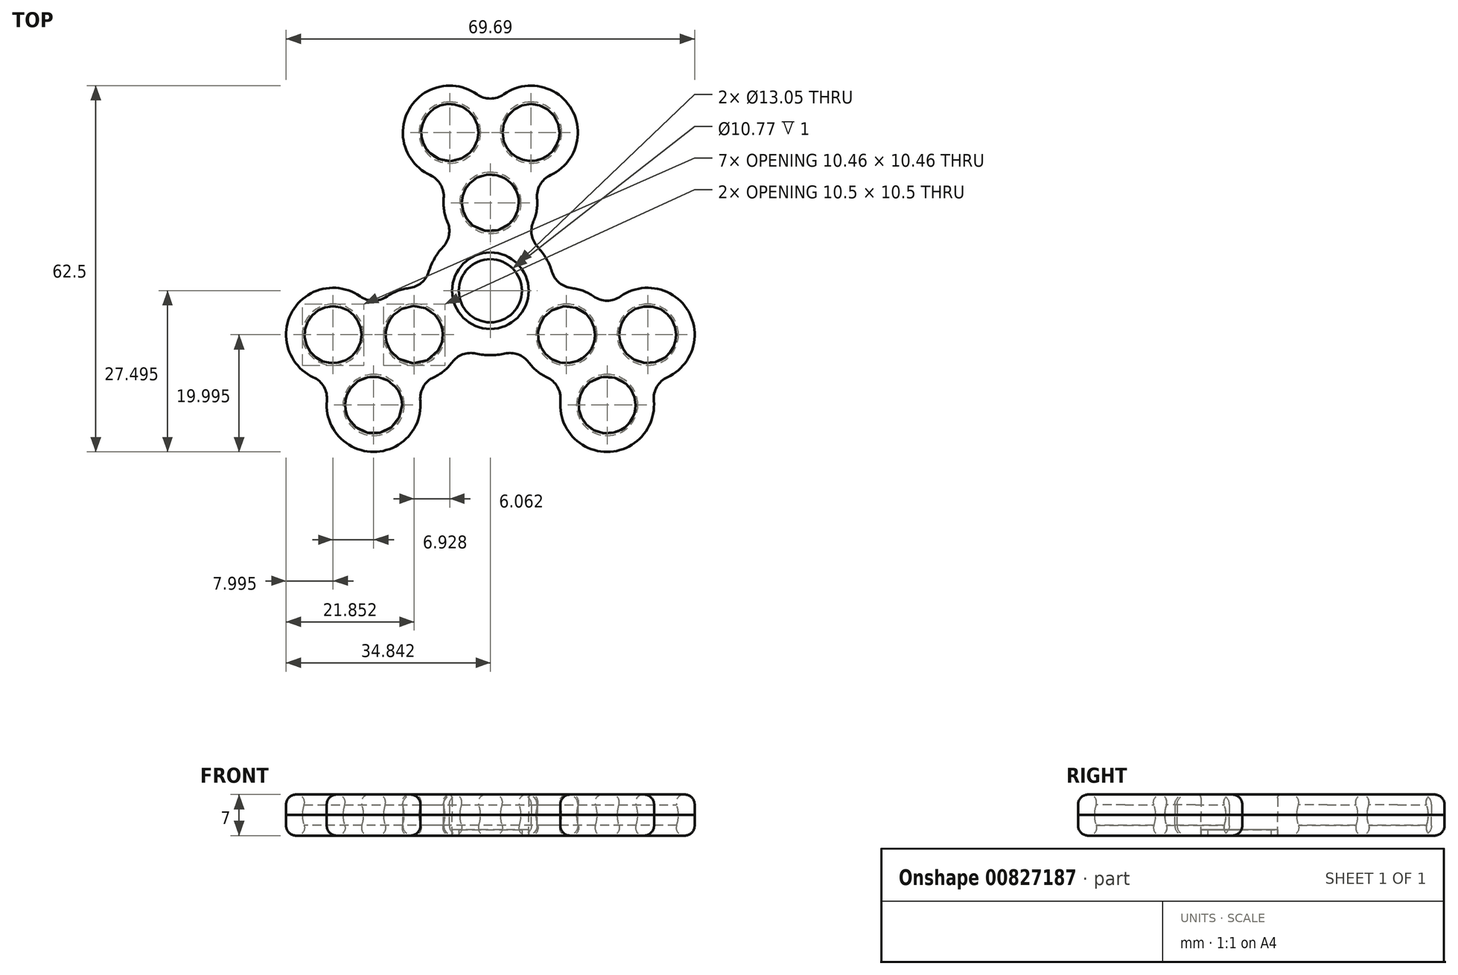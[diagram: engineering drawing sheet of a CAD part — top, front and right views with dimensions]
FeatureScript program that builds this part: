
annotation { "Feature Type Name" : "Feature", "Feature Type Description" : "" }
export const myFeature = defineFeature(function(context is Context, id is Id, definition is map)
    precondition{}
    {
        {
            var Q0;
            Q0=qCreatedBy(makeId("Top.planeOp"),FACE);
            var sketch = newSketch(context, id + "F0", { "sketchPlane" : qUnion([Q0])});
            skCircle(sketch, "E0", {"center": v(73.24, 0.6) * mm, "radius": 6.53 * mm});
            skCircle(sketch, "E1", {"center": v(73.24, 15.6) * mm, "radius": 2.5 * mm});
            skCircle(sketch, "E2", {"center": v(60.25, -6.9) * mm, "radius": 2.5 * mm});
            skCircle(sketch, "E3", {"center": v(86.23, -6.9) * mm, "radius": 2.5 * mm});
            skCircle(sketch, "E4", {"center": v(80.17, 27.6) * mm, "radius": 2.5 * mm});
            skCircle(sketch, "E5", {"center": v(66.31, 27.6) * mm, "radius": 2.5 * mm});
            skCircle(sketch, "E6", {"center": v(46.4, -6.9) * mm, "radius": 2.5 * mm});
            skCircle(sketch, "E7", {"center": v(53.32, -18.9) * mm, "radius": 2.5 * mm});
            skCircle(sketch, "E8", {"center": v(93.16, -18.9) * mm, "radius": 2.5 * mm});
            skCircle(sketch, "E9", {"center": v(100.09, -6.9) * mm, "radius": 2.5 * mm});
            skPoint(sketch, "E10.visualSharp", {"position": v(73.24, 28.6) * mm});
            skPoint(sketch, "E11.visualSharp", {"position": v(68.91, 21.1) * mm});
            skPoint(sketch, "E12.visualSharp", {"position": v(77.57, 21.1) * mm});
            skPoint(sketch, "E13.visualSharp", {"position": v(63.31, -0.6) * mm});
            skPoint(sketch, "E14.visualSharp", {"position": v(67.23, -7.39) * mm});
            skPoint(sketch, "E15.visualSharp", {"position": v(79.25, -7.39) * mm});
            skPoint(sketch, "E16.visualSharp", {"position": v(83.17, -0.6) * mm});
            skPoint(sketch, "E17.visualSharp", {"position": v(77.16, 9.8) * mm});
            skPoint(sketch, "E18.visualSharp", {"position": v(69.32, 9.8) * mm});
            skArc(sketch, "E19.0", {"start": v(59.36, 1.05) * mm, "mid": v(57.4, 0.58) * mm, "end": v(55.63, -0.36) * mm});
            skArc(sketch, "E19.1", {"start": v(65.18, 8.09) * mm, "mid": v(63.72, 6.1) * mm, "end": v(62.73, 3.85) * mm});
            skArc(sketch, "E19.2", {"start": v(65.28, 16.34) * mm, "mid": v(65.34, 14.33) * mm, "end": v(65.9, 12.4) * mm});
            skArc(sketch, "E19.3", {"start": v(70.93, 34.14) * mm, "mid": v(59.39, 31.6) * mm, "end": v(62.97, 20.34) * mm});
            skArc(sketch, "E19.4", {"start": v(79.8, -11.64) * mm, "mid": v(81.18, -13.1) * mm, "end": v(82.88, -14.16) * mm});
            skArc(sketch, "E19.5", {"start": v(70.8, -10.12) * mm, "mid": v(73.24, -10.4) * mm, "end": v(75.69, -10.12) * mm});
            skArc(sketch, "E19.6", {"start": v(63.6, -14.16) * mm, "mid": v(65.3, -13.1) * mm, "end": v(66.69, -11.64) * mm});
            skArc(sketch, "E19.7", {"start": v(45.36, -18.16) * mm, "mid": v(53.32, -26.9) * mm, "end": v(61.29, -18.16) * mm});
            skArc(sketch, "E19.8", {"start": v(85.2, -18.16) * mm, "mid": v(93.16, -26.9) * mm, "end": v(101.13, -18.16) * mm});
            skArc(sketch, "E19.9", {"start": v(103.44, -14.16) * mm, "mid": v(107.02, -2.9) * mm, "end": v(95.47, -0.36) * mm});
            skArc(sketch, "E19.10", {"start": v(90.85, -0.36) * mm, "mid": v(89.08, 0.58) * mm, "end": v(87.13, 1.05) * mm});
            skArc(sketch, "E19.11", {"start": v(83.75, 3.85) * mm, "mid": v(82.77, 6.1) * mm, "end": v(81.3, 8.09) * mm});
            skArc(sketch, "E19.12", {"start": v(51.01, -0.36) * mm, "mid": v(39.47, -2.9) * mm, "end": v(43.05, -14.16) * mm});
            skArc(sketch, "E19.13", {"start": v(80.57, 12.4) * mm, "mid": v(81.14, 14.33) * mm, "end": v(81.2, 16.34) * mm});
            skArc(sketch, "E19.14", {"start": v(83.52, 20.34) * mm, "mid": v(87.1, 31.6) * mm, "end": v(75.55, 34.14) * mm});
            skArc(sketch, "E20.0", {"start": v(45.36, -18.16) * mm, "mid": v(44.84, -15.8) * mm, "end": v(43.05, -14.16) * mm});
            skArc(sketch, "E21.0", {"start": v(63.6, -14.16) * mm, "mid": v(61.8, -15.8) * mm, "end": v(61.29, -18.16) * mm});
            skArc(sketch, "E22.0", {"start": v(70.8, -10.12) * mm, "mid": v(68.52, -10.27) * mm, "end": v(66.69, -11.64) * mm});
            skArc(sketch, "E23.0", {"start": v(79.8, -11.64) * mm, "mid": v(77.97, -10.27) * mm, "end": v(75.69, -10.12) * mm});
            skArc(sketch, "E24.0", {"start": v(85.2, -18.16) * mm, "mid": v(84.68, -15.8) * mm, "end": v(82.88, -14.16) * mm});
            skArc(sketch, "E25.0", {"start": v(103.44, -14.16) * mm, "mid": v(101.65, -15.8) * mm, "end": v(101.13, -18.16) * mm});
            skArc(sketch, "E26.0", {"start": v(90.85, -0.36) * mm, "mid": v(93.16, -1.1) * mm, "end": v(95.47, -0.36) * mm});
            skArc(sketch, "E27.0", {"start": v(83.75, 3.85) * mm, "mid": v(85.02, 1.95) * mm, "end": v(87.13, 1.05) * mm});
            skArc(sketch, "E28.0", {"start": v(80.57, 12.4) * mm, "mid": v(80.3, 10.14) * mm, "end": v(81.3, 8.09) * mm});
            skArc(sketch, "E29.0", {"start": v(83.52, 20.34) * mm, "mid": v(81.73, 18.7) * mm, "end": v(81.2, 16.34) * mm});
            skArc(sketch, "E30.0", {"start": v(65.28, 16.34) * mm, "mid": v(64.76, 18.7) * mm, "end": v(62.97, 20.34) * mm});
            skArc(sketch, "E31.0", {"start": v(65.18, 8.09) * mm, "mid": v(66.19, 10.14) * mm, "end": v(65.9, 12.4) * mm});
            skArc(sketch, "E32.0", {"start": v(59.36, 1.05) * mm, "mid": v(61.46, 1.95) * mm, "end": v(62.73, 3.85) * mm});
            skArc(sketch, "E33.0", {"start": v(51.01, -0.36) * mm, "mid": v(53.32, -1.1) * mm, "end": v(55.63, -0.36) * mm});
            skArc(sketch, "E34.0", {"start": v(70.93, 34.14) * mm, "mid": v(73.24, 33.4) * mm, "end": v(75.55, 34.14) * mm});
            skSolve(sketch);
        }
        {
            var Q0;
            Q0=qSketchRegion(id+"F0",true);
            extrude(context, id + "F1", {"entities" : qUnion([Q0]), "depth" : 3.5 * mm, "offsetDistance" : 25 * mm});
        }
        {
            var Q0;
            Q0=makeQuery(id+"F0.imprint","IMPRINT",FACE,{"disambiguationData":[TD([[makeQuery(id+"F0.imprint","IMPRINT",EDGE,{"derivedFrom":sQuery(id+"F0.wireOp",EDGE,"E0")}),-1.0]])]});
            extrude(context, id + "F2", {"entities" : qUnion([Q0]), "oppositeDirection" : true, "depth" : 3.5 * mm, "offsetDistance" : 25 * mm});
        }
        {
            var Q0;
            Q0=makeQuery(id+"F2.opExtrude","CAP_FACE",FACE,{"disambiguationData":[OSD([sQuery(id+"F0.wireOp",EDGE,"E0"),sQuery(id+"F0.wireOp",EDGE,"tXCEuyxa-6lNA-QPCA-4HXf-ApKYShcEb0Yf"),sQuery(id+"F0.wireOp",EDGE,"E1"),sQuery(id+"F0.wireOp",EDGE,"E2"),sQuery(id+"F0.wireOp",EDGE,"E3"),sQuery(id+"F0.wireOp",EDGE,"E4"),sQuery(id+"F0.wireOp",EDGE,"E5"),sQuery(id+"F0.wireOp",EDGE,"E6"),sQuery(id+"F0.wireOp",EDGE,"E7"),sQuery(id+"F0.wireOp",EDGE,"E8"),sQuery(id+"F0.wireOp",EDGE,"E9"),sQuery(id+"F0.wireOp",EDGE,"0kcF6Lq4-WqBE-dODE-wINV-nyZN5JArXVcS"),sQuery(id+"F0.wireOp",EDGE,"VSrMeVpB-pvXp-ETii-wjF9-Px2PqwZYQnOt"),sQuery(id+"F0.wireOp",EDGE,"OGzEMItw-FQCu-QhKJ-kTiP-AlfaDmg1CYfA"),sQuery(id+"F0.wireOp",EDGE,"E10.filletArc"),sQuery(id+"F0.wireOp",EDGE,"E11.filletArc"),sQuery(id+"F0.wireOp",EDGE,"E12.filletArc"),sQuery(id+"F0.wireOp",EDGE,"61869019-6ff7-477d-8c79-2028de4a396b.trimOffspring"),sQuery(id+"F0.wireOp",EDGE,"b39f1e7b-d492-47c6-a918-6e9c5b166b17"),sQuery(id+"F0.wireOp",EDGE,"9a7d06a7-665d-4e92-ad9d-959fca317462"),sQuery(id+"F0.wireOp",EDGE,"db31c51f-78d2-4091-9bd3-34a254103f45"),sQuery(id+"F0.wireOp",EDGE,"aaf24792-0303-4d5f-86de-c3b2a19fc74e.filletArc"),sQuery(id+"F0.wireOp",EDGE,"5ffe84d5-8cdf-4c2e-9e98-3655a6b86056.filletArc"),sQuery(id+"F0.wireOp",EDGE,"e8945d06-678d-4789-81f5-b1335d2624b7.filletArc"),sQuery(id+"F0.wireOp",EDGE,"a0b45458-2819-4e46-80a9-56e3c7e3f3b4.trimOffspring"),sQuery(id+"F0.wireOp",EDGE,"bf295548-413a-4249-b2ed-de7f7c0a0b82"),sQuery(id+"F0.wireOp",EDGE,"b03dbe81-5cdf-4ba7-a8f7-bb7ec46ab3a8"),sQuery(id+"F0.wireOp",EDGE,"b0d05724-446d-4885-847a-915c569f1139"),sQuery(id+"F0.wireOp",EDGE,"608d76ae-a745-4fd0-ae95-f5732494cd55.filletArc"),sQuery(id+"F0.wireOp",EDGE,"a41367dd-7dbd-4f08-888b-74168a8e5936.filletArc"),sQuery(id+"F0.wireOp",EDGE,"84e31002-7089-4eef-81a0-79c8965d61ed.filletArc"),sQuery(id+"F0.wireOp",EDGE,"1335fa2d-2410-4889-a90b-ae026db059b2.trimOffspring"),sQuery(id+"F0.wireOp",EDGE,"81157b49-ae94-446f-8b4e-5ce1e116e724.trimOffspring"),sQuery(id+"F0.wireOp",EDGE,"4f1c551e-3bfd-48a9-873a-6291d27f8455.trimOffspring"),sQuery(id+"F0.wireOp",EDGE,"E13.filletArc"),sQuery(id+"F0.wireOp",EDGE,"E14.filletArc"),sQuery(id+"F0.wireOp",EDGE,"E15.filletArc"),sQuery(id+"F0.wireOp",EDGE,"E16.filletArc"),sQuery(id+"F0.wireOp",EDGE,"E17.filletArc"),sQuery(id+"F0.wireOp",EDGE,"E18.filletArc")])],"isStart":true});
            var sketch = newSketch(context, id + "F3", { "sketchPlane" : qUnion([Q0])});
            skLineSegment(sketch, "E35", {"start": v(53.32, -18.9) * mm, "end": v(53.32, -24.12) * mm});
            skLineSegment(sketch, "E36", {"start": v(53.32, -18.9) * mm, "end": v(53.32, -13.66) * mm});
            skArc(sketch, "E37", {"start": v(53.32, -13.66) * mm, "mid": v(48.1, -18.9) * mm, "end": v(53.32, -24.12) * mm});
            skSolve(sketch);
        }
        {
            var Q0;
            Q0 = qSketchRegion(id + "F3", true);
            var Q1;
            Q1=sQuery(id+"F3.wireOp",EDGE,"E36");
            revolve(context, id + "F4", {"surfaceOperationType" : NewSurfaceOperationType.NEW, "entities" : qUnion([Q0]), "axis" : qUnion([Q1]), "revolveType" : RevolveType.FULL});
        }
        {
            var Q0;
            Q0=makeQuery(id+"F2.opExtrude","CAP_FACE",FACE,{"disambiguationData":[OSD([sQuery(id+"F0.wireOp",EDGE,"E0"),sQuery(id+"F0.wireOp",EDGE,"tXCEuyxa-6lNA-QPCA-4HXf-ApKYShcEb0Yf"),sQuery(id+"F0.wireOp",EDGE,"E1"),sQuery(id+"F0.wireOp",EDGE,"E2"),sQuery(id+"F0.wireOp",EDGE,"E3"),sQuery(id+"F0.wireOp",EDGE,"E4"),sQuery(id+"F0.wireOp",EDGE,"E5"),sQuery(id+"F0.wireOp",EDGE,"E6"),sQuery(id+"F0.wireOp",EDGE,"E7"),sQuery(id+"F0.wireOp",EDGE,"E8"),sQuery(id+"F0.wireOp",EDGE,"E9"),sQuery(id+"F0.wireOp",EDGE,"0kcF6Lq4-WqBE-dODE-wINV-nyZN5JArXVcS"),sQuery(id+"F0.wireOp",EDGE,"VSrMeVpB-pvXp-ETii-wjF9-Px2PqwZYQnOt"),sQuery(id+"F0.wireOp",EDGE,"OGzEMItw-FQCu-QhKJ-kTiP-AlfaDmg1CYfA"),sQuery(id+"F0.wireOp",EDGE,"E10.filletArc"),sQuery(id+"F0.wireOp",EDGE,"E11.filletArc"),sQuery(id+"F0.wireOp",EDGE,"E12.filletArc"),sQuery(id+"F0.wireOp",EDGE,"61869019-6ff7-477d-8c79-2028de4a396b.trimOffspring"),sQuery(id+"F0.wireOp",EDGE,"b39f1e7b-d492-47c6-a918-6e9c5b166b17"),sQuery(id+"F0.wireOp",EDGE,"9a7d06a7-665d-4e92-ad9d-959fca317462"),sQuery(id+"F0.wireOp",EDGE,"db31c51f-78d2-4091-9bd3-34a254103f45"),sQuery(id+"F0.wireOp",EDGE,"aaf24792-0303-4d5f-86de-c3b2a19fc74e.filletArc"),sQuery(id+"F0.wireOp",EDGE,"5ffe84d5-8cdf-4c2e-9e98-3655a6b86056.filletArc"),sQuery(id+"F0.wireOp",EDGE,"e8945d06-678d-4789-81f5-b1335d2624b7.filletArc"),sQuery(id+"F0.wireOp",EDGE,"a0b45458-2819-4e46-80a9-56e3c7e3f3b4.trimOffspring"),sQuery(id+"F0.wireOp",EDGE,"bf295548-413a-4249-b2ed-de7f7c0a0b82"),sQuery(id+"F0.wireOp",EDGE,"b03dbe81-5cdf-4ba7-a8f7-bb7ec46ab3a8"),sQuery(id+"F0.wireOp",EDGE,"b0d05724-446d-4885-847a-915c569f1139"),sQuery(id+"F0.wireOp",EDGE,"608d76ae-a745-4fd0-ae95-f5732494cd55.filletArc"),sQuery(id+"F0.wireOp",EDGE,"a41367dd-7dbd-4f08-888b-74168a8e5936.filletArc"),sQuery(id+"F0.wireOp",EDGE,"84e31002-7089-4eef-81a0-79c8965d61ed.filletArc"),sQuery(id+"F0.wireOp",EDGE,"1335fa2d-2410-4889-a90b-ae026db059b2.trimOffspring"),sQuery(id+"F0.wireOp",EDGE,"81157b49-ae94-446f-8b4e-5ce1e116e724.trimOffspring"),sQuery(id+"F0.wireOp",EDGE,"4f1c551e-3bfd-48a9-873a-6291d27f8455.trimOffspring"),sQuery(id+"F0.wireOp",EDGE,"E13.filletArc"),sQuery(id+"F0.wireOp",EDGE,"E14.filletArc"),sQuery(id+"F0.wireOp",EDGE,"E15.filletArc"),sQuery(id+"F0.wireOp",EDGE,"E16.filletArc"),sQuery(id+"F0.wireOp",EDGE,"E17.filletArc"),sQuery(id+"F0.wireOp",EDGE,"E18.filletArc")])],"isStart":true});
            var sketch = newSketch(context, id + "F5", { "sketchPlane" : qUnion([Q0])});
            skLineSegment(sketch, "E38", {"start": v(60.25, -6.9) * mm, "end": v(60.25, -12.14) * mm});
            skLineSegment(sketch, "E39", {"start": v(60.25, -6.9) * mm, "end": v(60.25, -1.64) * mm});
            skArc(sketch, "E40", {"start": v(60.25, -1.64) * mm, "mid": v(55, -6.9) * mm, "end": v(60.25, -12.14) * mm});
            skSolve(sketch);
        }
        {
            var Q0;
            Q0=makeQuery(id+"F2.opExtrude","CAP_FACE",FACE,{"disambiguationData":[OSD([sQuery(id+"F0.wireOp",EDGE,"E0"),sQuery(id+"F0.wireOp",EDGE,"tXCEuyxa-6lNA-QPCA-4HXf-ApKYShcEb0Yf"),sQuery(id+"F0.wireOp",EDGE,"E1"),sQuery(id+"F0.wireOp",EDGE,"E2"),sQuery(id+"F0.wireOp",EDGE,"E3"),sQuery(id+"F0.wireOp",EDGE,"E4"),sQuery(id+"F0.wireOp",EDGE,"E5"),sQuery(id+"F0.wireOp",EDGE,"E6"),sQuery(id+"F0.wireOp",EDGE,"E7"),sQuery(id+"F0.wireOp",EDGE,"E8"),sQuery(id+"F0.wireOp",EDGE,"E9"),sQuery(id+"F0.wireOp",EDGE,"0kcF6Lq4-WqBE-dODE-wINV-nyZN5JArXVcS"),sQuery(id+"F0.wireOp",EDGE,"VSrMeVpB-pvXp-ETii-wjF9-Px2PqwZYQnOt"),sQuery(id+"F0.wireOp",EDGE,"OGzEMItw-FQCu-QhKJ-kTiP-AlfaDmg1CYfA"),sQuery(id+"F0.wireOp",EDGE,"E10.filletArc"),sQuery(id+"F0.wireOp",EDGE,"E11.filletArc"),sQuery(id+"F0.wireOp",EDGE,"E12.filletArc"),sQuery(id+"F0.wireOp",EDGE,"61869019-6ff7-477d-8c79-2028de4a396b.trimOffspring"),sQuery(id+"F0.wireOp",EDGE,"b39f1e7b-d492-47c6-a918-6e9c5b166b17"),sQuery(id+"F0.wireOp",EDGE,"9a7d06a7-665d-4e92-ad9d-959fca317462"),sQuery(id+"F0.wireOp",EDGE,"db31c51f-78d2-4091-9bd3-34a254103f45"),sQuery(id+"F0.wireOp",EDGE,"aaf24792-0303-4d5f-86de-c3b2a19fc74e.filletArc"),sQuery(id+"F0.wireOp",EDGE,"5ffe84d5-8cdf-4c2e-9e98-3655a6b86056.filletArc"),sQuery(id+"F0.wireOp",EDGE,"e8945d06-678d-4789-81f5-b1335d2624b7.filletArc"),sQuery(id+"F0.wireOp",EDGE,"a0b45458-2819-4e46-80a9-56e3c7e3f3b4.trimOffspring"),sQuery(id+"F0.wireOp",EDGE,"bf295548-413a-4249-b2ed-de7f7c0a0b82"),sQuery(id+"F0.wireOp",EDGE,"b03dbe81-5cdf-4ba7-a8f7-bb7ec46ab3a8"),sQuery(id+"F0.wireOp",EDGE,"b0d05724-446d-4885-847a-915c569f1139"),sQuery(id+"F0.wireOp",EDGE,"608d76ae-a745-4fd0-ae95-f5732494cd55.filletArc"),sQuery(id+"F0.wireOp",EDGE,"a41367dd-7dbd-4f08-888b-74168a8e5936.filletArc"),sQuery(id+"F0.wireOp",EDGE,"84e31002-7089-4eef-81a0-79c8965d61ed.filletArc"),sQuery(id+"F0.wireOp",EDGE,"1335fa2d-2410-4889-a90b-ae026db059b2.trimOffspring"),sQuery(id+"F0.wireOp",EDGE,"81157b49-ae94-446f-8b4e-5ce1e116e724.trimOffspring"),sQuery(id+"F0.wireOp",EDGE,"4f1c551e-3bfd-48a9-873a-6291d27f8455.trimOffspring"),sQuery(id+"F0.wireOp",EDGE,"E13.filletArc"),sQuery(id+"F0.wireOp",EDGE,"E14.filletArc"),sQuery(id+"F0.wireOp",EDGE,"E15.filletArc"),sQuery(id+"F0.wireOp",EDGE,"E16.filletArc"),sQuery(id+"F0.wireOp",EDGE,"E17.filletArc"),sQuery(id+"F0.wireOp",EDGE,"E18.filletArc")])],"isStart":true});
            var sketch = newSketch(context, id + "F6", { "sketchPlane" : qUnion([Q0])});
            skLineSegment(sketch, "E41", {"start": v(93.16, -18.9) * mm, "end": v(93.16, -24.12) * mm});
            skArc(sketch, "E42", {"start": v(93.16, -13.66) * mm, "mid": v(87.93, -18.9) * mm, "end": v(93.16, -24.12) * mm});
            skLineSegment(sketch, "E43", {"start": v(93.16, -18.9) * mm, "end": v(93.16, -13.66) * mm});
            skSolve(sketch);
        }
        {
            var Q0;
            Q0 = qSketchRegion(id + "F6", true);
            var Q1;
            Q1=sQuery(id+"F6.wireOp",EDGE,"E43");
            revolve(context, id + "F7", {"surfaceOperationType" : NewSurfaceOperationType.NEW, "entities" : qUnion([Q0]), "axis" : qUnion([Q1]), "revolveType" : RevolveType.FULL});
        }
        {
            var Q0;
            Q0=makeQuery(id+"F2.opExtrude","CAP_FACE",FACE,{"disambiguationData":[OSD([sQuery(id+"F0.wireOp",EDGE,"E0"),sQuery(id+"F0.wireOp",EDGE,"tXCEuyxa-6lNA-QPCA-4HXf-ApKYShcEb0Yf"),sQuery(id+"F0.wireOp",EDGE,"E1"),sQuery(id+"F0.wireOp",EDGE,"E2"),sQuery(id+"F0.wireOp",EDGE,"E3"),sQuery(id+"F0.wireOp",EDGE,"E4"),sQuery(id+"F0.wireOp",EDGE,"E5"),sQuery(id+"F0.wireOp",EDGE,"E6"),sQuery(id+"F0.wireOp",EDGE,"E7"),sQuery(id+"F0.wireOp",EDGE,"E8"),sQuery(id+"F0.wireOp",EDGE,"E9"),sQuery(id+"F0.wireOp",EDGE,"0kcF6Lq4-WqBE-dODE-wINV-nyZN5JArXVcS"),sQuery(id+"F0.wireOp",EDGE,"VSrMeVpB-pvXp-ETii-wjF9-Px2PqwZYQnOt"),sQuery(id+"F0.wireOp",EDGE,"OGzEMItw-FQCu-QhKJ-kTiP-AlfaDmg1CYfA"),sQuery(id+"F0.wireOp",EDGE,"E10.filletArc"),sQuery(id+"F0.wireOp",EDGE,"E11.filletArc"),sQuery(id+"F0.wireOp",EDGE,"E12.filletArc"),sQuery(id+"F0.wireOp",EDGE,"61869019-6ff7-477d-8c79-2028de4a396b.trimOffspring"),sQuery(id+"F0.wireOp",EDGE,"b39f1e7b-d492-47c6-a918-6e9c5b166b17"),sQuery(id+"F0.wireOp",EDGE,"9a7d06a7-665d-4e92-ad9d-959fca317462"),sQuery(id+"F0.wireOp",EDGE,"db31c51f-78d2-4091-9bd3-34a254103f45"),sQuery(id+"F0.wireOp",EDGE,"aaf24792-0303-4d5f-86de-c3b2a19fc74e.filletArc"),sQuery(id+"F0.wireOp",EDGE,"5ffe84d5-8cdf-4c2e-9e98-3655a6b86056.filletArc"),sQuery(id+"F0.wireOp",EDGE,"e8945d06-678d-4789-81f5-b1335d2624b7.filletArc"),sQuery(id+"F0.wireOp",EDGE,"a0b45458-2819-4e46-80a9-56e3c7e3f3b4.trimOffspring"),sQuery(id+"F0.wireOp",EDGE,"bf295548-413a-4249-b2ed-de7f7c0a0b82"),sQuery(id+"F0.wireOp",EDGE,"b03dbe81-5cdf-4ba7-a8f7-bb7ec46ab3a8"),sQuery(id+"F0.wireOp",EDGE,"b0d05724-446d-4885-847a-915c569f1139"),sQuery(id+"F0.wireOp",EDGE,"608d76ae-a745-4fd0-ae95-f5732494cd55.filletArc"),sQuery(id+"F0.wireOp",EDGE,"a41367dd-7dbd-4f08-888b-74168a8e5936.filletArc"),sQuery(id+"F0.wireOp",EDGE,"84e31002-7089-4eef-81a0-79c8965d61ed.filletArc"),sQuery(id+"F0.wireOp",EDGE,"1335fa2d-2410-4889-a90b-ae026db059b2.trimOffspring"),sQuery(id+"F0.wireOp",EDGE,"81157b49-ae94-446f-8b4e-5ce1e116e724.trimOffspring"),sQuery(id+"F0.wireOp",EDGE,"4f1c551e-3bfd-48a9-873a-6291d27f8455.trimOffspring"),sQuery(id+"F0.wireOp",EDGE,"E13.filletArc"),sQuery(id+"F0.wireOp",EDGE,"E14.filletArc"),sQuery(id+"F0.wireOp",EDGE,"E15.filletArc"),sQuery(id+"F0.wireOp",EDGE,"E16.filletArc"),sQuery(id+"F0.wireOp",EDGE,"E17.filletArc"),sQuery(id+"F0.wireOp",EDGE,"E18.filletArc")])],"isStart":true});
            var sketch = newSketch(context, id + "F8", { "sketchPlane" : qUnion([Q0])});
            skLineSegment(sketch, "E44", {"start": v(86.23, -6.9) * mm, "end": v(86.23, -12.12) * mm});
            skArc(sketch, "E45", {"start": v(86.23, -1.66) * mm, "mid": v(81, -6.9) * mm, "end": v(86.23, -12.12) * mm});
            skLineSegment(sketch, "E46", {"start": v(86.23, -6.9) * mm, "end": v(86.23, -1.66) * mm});
            skSolve(sketch);
        }
        {
            var Q0;
            Q0 = qSketchRegion(id + "F8", true);
            var Q1;
            Q1=sQuery(id+"F8.wireOp",EDGE,"E46");
            revolve(context, id + "F9", {"surfaceOperationType" : NewSurfaceOperationType.NEW, "entities" : qUnion([Q0]), "axis" : qUnion([Q1]), "revolveType" : RevolveType.FULL});
        }
        {
            var Q0;
            Q0=makeQuery(id+"F2.opExtrude","CAP_FACE",FACE,{"disambiguationData":[OSD([sQuery(id+"F0.wireOp",EDGE,"E0"),sQuery(id+"F0.wireOp",EDGE,"tXCEuyxa-6lNA-QPCA-4HXf-ApKYShcEb0Yf"),sQuery(id+"F0.wireOp",EDGE,"E1"),sQuery(id+"F0.wireOp",EDGE,"E2"),sQuery(id+"F0.wireOp",EDGE,"E3"),sQuery(id+"F0.wireOp",EDGE,"E4"),sQuery(id+"F0.wireOp",EDGE,"E5"),sQuery(id+"F0.wireOp",EDGE,"E6"),sQuery(id+"F0.wireOp",EDGE,"E7"),sQuery(id+"F0.wireOp",EDGE,"E8"),sQuery(id+"F0.wireOp",EDGE,"E9"),sQuery(id+"F0.wireOp",EDGE,"0kcF6Lq4-WqBE-dODE-wINV-nyZN5JArXVcS"),sQuery(id+"F0.wireOp",EDGE,"VSrMeVpB-pvXp-ETii-wjF9-Px2PqwZYQnOt"),sQuery(id+"F0.wireOp",EDGE,"OGzEMItw-FQCu-QhKJ-kTiP-AlfaDmg1CYfA"),sQuery(id+"F0.wireOp",EDGE,"E10.filletArc"),sQuery(id+"F0.wireOp",EDGE,"E11.filletArc"),sQuery(id+"F0.wireOp",EDGE,"E12.filletArc"),sQuery(id+"F0.wireOp",EDGE,"61869019-6ff7-477d-8c79-2028de4a396b.trimOffspring"),sQuery(id+"F0.wireOp",EDGE,"b39f1e7b-d492-47c6-a918-6e9c5b166b17"),sQuery(id+"F0.wireOp",EDGE,"9a7d06a7-665d-4e92-ad9d-959fca317462"),sQuery(id+"F0.wireOp",EDGE,"db31c51f-78d2-4091-9bd3-34a254103f45"),sQuery(id+"F0.wireOp",EDGE,"aaf24792-0303-4d5f-86de-c3b2a19fc74e.filletArc"),sQuery(id+"F0.wireOp",EDGE,"5ffe84d5-8cdf-4c2e-9e98-3655a6b86056.filletArc"),sQuery(id+"F0.wireOp",EDGE,"e8945d06-678d-4789-81f5-b1335d2624b7.filletArc"),sQuery(id+"F0.wireOp",EDGE,"a0b45458-2819-4e46-80a9-56e3c7e3f3b4.trimOffspring"),sQuery(id+"F0.wireOp",EDGE,"bf295548-413a-4249-b2ed-de7f7c0a0b82"),sQuery(id+"F0.wireOp",EDGE,"b03dbe81-5cdf-4ba7-a8f7-bb7ec46ab3a8"),sQuery(id+"F0.wireOp",EDGE,"b0d05724-446d-4885-847a-915c569f1139"),sQuery(id+"F0.wireOp",EDGE,"608d76ae-a745-4fd0-ae95-f5732494cd55.filletArc"),sQuery(id+"F0.wireOp",EDGE,"a41367dd-7dbd-4f08-888b-74168a8e5936.filletArc"),sQuery(id+"F0.wireOp",EDGE,"84e31002-7089-4eef-81a0-79c8965d61ed.filletArc"),sQuery(id+"F0.wireOp",EDGE,"1335fa2d-2410-4889-a90b-ae026db059b2.trimOffspring"),sQuery(id+"F0.wireOp",EDGE,"81157b49-ae94-446f-8b4e-5ce1e116e724.trimOffspring"),sQuery(id+"F0.wireOp",EDGE,"4f1c551e-3bfd-48a9-873a-6291d27f8455.trimOffspring"),sQuery(id+"F0.wireOp",EDGE,"E13.filletArc"),sQuery(id+"F0.wireOp",EDGE,"E14.filletArc"),sQuery(id+"F0.wireOp",EDGE,"E15.filletArc"),sQuery(id+"F0.wireOp",EDGE,"E16.filletArc"),sQuery(id+"F0.wireOp",EDGE,"E17.filletArc"),sQuery(id+"F0.wireOp",EDGE,"E18.filletArc")])],"isStart":true});
            var sketch = newSketch(context, id + "F10", { "sketchPlane" : qUnion([Q0])});
            skLineSegment(sketch, "E47", {"start": v(100.09, -6.9) * mm, "end": v(100.09, -12.12) * mm});
            skArc(sketch, "E48", {"start": v(100.09, -1.66) * mm, "mid": v(94.86, -6.9) * mm, "end": v(100.09, -12.12) * mm});
            skLineSegment(sketch, "E49", {"start": v(100.09, -6.9) * mm, "end": v(100.09, -1.66) * mm});
            skSolve(sketch);
        }
        {
            var Q0;
            Q0 = qSketchRegion(id + "F10", true);
            var Q1;
            Q1=sQuery(id+"F10.wireOp",EDGE,"E47");
            revolve(context, id + "F11", {"surfaceOperationType" : NewSurfaceOperationType.NEW, "entities" : qUnion([Q0]), "axis" : qUnion([Q1]), "revolveType" : RevolveType.FULL});
        }
        {
            var Q0;
            Q0=makeQuery(id+"F2.opExtrude","CAP_FACE",FACE,{"disambiguationData":[OSD([sQuery(id+"F0.wireOp",EDGE,"E0"),sQuery(id+"F0.wireOp",EDGE,"tXCEuyxa-6lNA-QPCA-4HXf-ApKYShcEb0Yf"),sQuery(id+"F0.wireOp",EDGE,"E1"),sQuery(id+"F0.wireOp",EDGE,"E2"),sQuery(id+"F0.wireOp",EDGE,"E3"),sQuery(id+"F0.wireOp",EDGE,"E4"),sQuery(id+"F0.wireOp",EDGE,"E5"),sQuery(id+"F0.wireOp",EDGE,"E6"),sQuery(id+"F0.wireOp",EDGE,"E7"),sQuery(id+"F0.wireOp",EDGE,"E8"),sQuery(id+"F0.wireOp",EDGE,"E9"),sQuery(id+"F0.wireOp",EDGE,"0kcF6Lq4-WqBE-dODE-wINV-nyZN5JArXVcS"),sQuery(id+"F0.wireOp",EDGE,"VSrMeVpB-pvXp-ETii-wjF9-Px2PqwZYQnOt"),sQuery(id+"F0.wireOp",EDGE,"OGzEMItw-FQCu-QhKJ-kTiP-AlfaDmg1CYfA"),sQuery(id+"F0.wireOp",EDGE,"E10.filletArc"),sQuery(id+"F0.wireOp",EDGE,"E11.filletArc"),sQuery(id+"F0.wireOp",EDGE,"E12.filletArc"),sQuery(id+"F0.wireOp",EDGE,"61869019-6ff7-477d-8c79-2028de4a396b.trimOffspring"),sQuery(id+"F0.wireOp",EDGE,"b39f1e7b-d492-47c6-a918-6e9c5b166b17"),sQuery(id+"F0.wireOp",EDGE,"9a7d06a7-665d-4e92-ad9d-959fca317462"),sQuery(id+"F0.wireOp",EDGE,"db31c51f-78d2-4091-9bd3-34a254103f45"),sQuery(id+"F0.wireOp",EDGE,"aaf24792-0303-4d5f-86de-c3b2a19fc74e.filletArc"),sQuery(id+"F0.wireOp",EDGE,"5ffe84d5-8cdf-4c2e-9e98-3655a6b86056.filletArc"),sQuery(id+"F0.wireOp",EDGE,"e8945d06-678d-4789-81f5-b1335d2624b7.filletArc"),sQuery(id+"F0.wireOp",EDGE,"a0b45458-2819-4e46-80a9-56e3c7e3f3b4.trimOffspring"),sQuery(id+"F0.wireOp",EDGE,"bf295548-413a-4249-b2ed-de7f7c0a0b82"),sQuery(id+"F0.wireOp",EDGE,"b03dbe81-5cdf-4ba7-a8f7-bb7ec46ab3a8"),sQuery(id+"F0.wireOp",EDGE,"b0d05724-446d-4885-847a-915c569f1139"),sQuery(id+"F0.wireOp",EDGE,"608d76ae-a745-4fd0-ae95-f5732494cd55.filletArc"),sQuery(id+"F0.wireOp",EDGE,"a41367dd-7dbd-4f08-888b-74168a8e5936.filletArc"),sQuery(id+"F0.wireOp",EDGE,"84e31002-7089-4eef-81a0-79c8965d61ed.filletArc"),sQuery(id+"F0.wireOp",EDGE,"1335fa2d-2410-4889-a90b-ae026db059b2.trimOffspring"),sQuery(id+"F0.wireOp",EDGE,"81157b49-ae94-446f-8b4e-5ce1e116e724.trimOffspring"),sQuery(id+"F0.wireOp",EDGE,"4f1c551e-3bfd-48a9-873a-6291d27f8455.trimOffspring"),sQuery(id+"F0.wireOp",EDGE,"E13.filletArc"),sQuery(id+"F0.wireOp",EDGE,"E14.filletArc"),sQuery(id+"F0.wireOp",EDGE,"E15.filletArc"),sQuery(id+"F0.wireOp",EDGE,"E16.filletArc"),sQuery(id+"F0.wireOp",EDGE,"E17.filletArc"),sQuery(id+"F0.wireOp",EDGE,"E18.filletArc")])],"isStart":true});
            var sketch = newSketch(context, id + "F12", { "sketchPlane" : qUnion([Q0])});
            skLineSegment(sketch, "E50", {"start": v(73.24, 15.6) * mm, "end": v(73.24, 10.38) * mm});
            skArc(sketch, "E51", {"start": v(73.24, 20.84) * mm, "mid": v(68.01, 15.6) * mm, "end": v(73.24, 10.38) * mm});
            skLineSegment(sketch, "E52", {"start": v(73.24, 15.6) * mm, "end": v(73.24, 20.84) * mm});
            skSolve(sketch);
        }
        {
            var Q0;
            Q0 = qSketchRegion(id + "F12", true);
            var Q1;
            Q1=sQuery(id+"F12.wireOp",EDGE,"E50");
            revolve(context, id + "F13", {"surfaceOperationType" : NewSurfaceOperationType.NEW, "entities" : qUnion([Q0]), "axis" : qUnion([Q1]), "revolveType" : RevolveType.FULL});
        }
        {
            var Q0;
            Q0=makeQuery(id+"F2.opExtrude","CAP_FACE",FACE,{"disambiguationData":[OSD([sQuery(id+"F0.wireOp",EDGE,"E0"),sQuery(id+"F0.wireOp",EDGE,"tXCEuyxa-6lNA-QPCA-4HXf-ApKYShcEb0Yf"),sQuery(id+"F0.wireOp",EDGE,"E1"),sQuery(id+"F0.wireOp",EDGE,"E2"),sQuery(id+"F0.wireOp",EDGE,"E3"),sQuery(id+"F0.wireOp",EDGE,"E4"),sQuery(id+"F0.wireOp",EDGE,"E5"),sQuery(id+"F0.wireOp",EDGE,"E6"),sQuery(id+"F0.wireOp",EDGE,"E7"),sQuery(id+"F0.wireOp",EDGE,"E8"),sQuery(id+"F0.wireOp",EDGE,"E9"),sQuery(id+"F0.wireOp",EDGE,"0kcF6Lq4-WqBE-dODE-wINV-nyZN5JArXVcS"),sQuery(id+"F0.wireOp",EDGE,"VSrMeVpB-pvXp-ETii-wjF9-Px2PqwZYQnOt"),sQuery(id+"F0.wireOp",EDGE,"OGzEMItw-FQCu-QhKJ-kTiP-AlfaDmg1CYfA"),sQuery(id+"F0.wireOp",EDGE,"E10.filletArc"),sQuery(id+"F0.wireOp",EDGE,"E11.filletArc"),sQuery(id+"F0.wireOp",EDGE,"E12.filletArc"),sQuery(id+"F0.wireOp",EDGE,"61869019-6ff7-477d-8c79-2028de4a396b.trimOffspring"),sQuery(id+"F0.wireOp",EDGE,"b39f1e7b-d492-47c6-a918-6e9c5b166b17"),sQuery(id+"F0.wireOp",EDGE,"9a7d06a7-665d-4e92-ad9d-959fca317462"),sQuery(id+"F0.wireOp",EDGE,"db31c51f-78d2-4091-9bd3-34a254103f45"),sQuery(id+"F0.wireOp",EDGE,"aaf24792-0303-4d5f-86de-c3b2a19fc74e.filletArc"),sQuery(id+"F0.wireOp",EDGE,"5ffe84d5-8cdf-4c2e-9e98-3655a6b86056.filletArc"),sQuery(id+"F0.wireOp",EDGE,"e8945d06-678d-4789-81f5-b1335d2624b7.filletArc"),sQuery(id+"F0.wireOp",EDGE,"a0b45458-2819-4e46-80a9-56e3c7e3f3b4.trimOffspring"),sQuery(id+"F0.wireOp",EDGE,"bf295548-413a-4249-b2ed-de7f7c0a0b82"),sQuery(id+"F0.wireOp",EDGE,"b03dbe81-5cdf-4ba7-a8f7-bb7ec46ab3a8"),sQuery(id+"F0.wireOp",EDGE,"b0d05724-446d-4885-847a-915c569f1139"),sQuery(id+"F0.wireOp",EDGE,"608d76ae-a745-4fd0-ae95-f5732494cd55.filletArc"),sQuery(id+"F0.wireOp",EDGE,"a41367dd-7dbd-4f08-888b-74168a8e5936.filletArc"),sQuery(id+"F0.wireOp",EDGE,"84e31002-7089-4eef-81a0-79c8965d61ed.filletArc"),sQuery(id+"F0.wireOp",EDGE,"1335fa2d-2410-4889-a90b-ae026db059b2.trimOffspring"),sQuery(id+"F0.wireOp",EDGE,"81157b49-ae94-446f-8b4e-5ce1e116e724.trimOffspring"),sQuery(id+"F0.wireOp",EDGE,"4f1c551e-3bfd-48a9-873a-6291d27f8455.trimOffspring"),sQuery(id+"F0.wireOp",EDGE,"E13.filletArc"),sQuery(id+"F0.wireOp",EDGE,"E14.filletArc"),sQuery(id+"F0.wireOp",EDGE,"E15.filletArc"),sQuery(id+"F0.wireOp",EDGE,"E16.filletArc"),sQuery(id+"F0.wireOp",EDGE,"E17.filletArc"),sQuery(id+"F0.wireOp",EDGE,"E18.filletArc")])],"isStart":true});
            var sketch = newSketch(context, id + "F14", { "sketchPlane" : qUnion([Q0])});
            skLineSegment(sketch, "E53", {"start": v(66.31, 27.6) * mm, "end": v(66.31, 22.36) * mm});
            skArc(sketch, "E54", {"start": v(66.31, 32.86) * mm, "mid": v(61.06, 27.6) * mm, "end": v(66.31, 22.36) * mm});
            skLineSegment(sketch, "E55", {"start": v(66.31, 27.6) * mm, "end": v(66.31, 32.86) * mm});
            skSolve(sketch);
        }
        {
            var Q0;
            Q0 = qSketchRegion(id + "F14", true);
            var Q1;
            Q1=sQuery(id+"F14.wireOp",EDGE,"E53");
            revolve(context, id + "F15", {"surfaceOperationType" : NewSurfaceOperationType.NEW, "entities" : qUnion([Q0]), "axis" : qUnion([Q1]), "revolveType" : RevolveType.FULL});
        }
        {
            var Q0;
            Q0=makeQuery(id+"F2.opExtrude","CAP_FACE",FACE,{"disambiguationData":[OSD([sQuery(id+"F0.wireOp",EDGE,"E0"),sQuery(id+"F0.wireOp",EDGE,"tXCEuyxa-6lNA-QPCA-4HXf-ApKYShcEb0Yf"),sQuery(id+"F0.wireOp",EDGE,"E1"),sQuery(id+"F0.wireOp",EDGE,"E2"),sQuery(id+"F0.wireOp",EDGE,"E3"),sQuery(id+"F0.wireOp",EDGE,"E4"),sQuery(id+"F0.wireOp",EDGE,"E5"),sQuery(id+"F0.wireOp",EDGE,"E6"),sQuery(id+"F0.wireOp",EDGE,"E7"),sQuery(id+"F0.wireOp",EDGE,"E8"),sQuery(id+"F0.wireOp",EDGE,"E9"),sQuery(id+"F0.wireOp",EDGE,"0kcF6Lq4-WqBE-dODE-wINV-nyZN5JArXVcS"),sQuery(id+"F0.wireOp",EDGE,"VSrMeVpB-pvXp-ETii-wjF9-Px2PqwZYQnOt"),sQuery(id+"F0.wireOp",EDGE,"OGzEMItw-FQCu-QhKJ-kTiP-AlfaDmg1CYfA"),sQuery(id+"F0.wireOp",EDGE,"E10.filletArc"),sQuery(id+"F0.wireOp",EDGE,"E11.filletArc"),sQuery(id+"F0.wireOp",EDGE,"E12.filletArc"),sQuery(id+"F0.wireOp",EDGE,"61869019-6ff7-477d-8c79-2028de4a396b.trimOffspring"),sQuery(id+"F0.wireOp",EDGE,"b39f1e7b-d492-47c6-a918-6e9c5b166b17"),sQuery(id+"F0.wireOp",EDGE,"9a7d06a7-665d-4e92-ad9d-959fca317462"),sQuery(id+"F0.wireOp",EDGE,"db31c51f-78d2-4091-9bd3-34a254103f45"),sQuery(id+"F0.wireOp",EDGE,"aaf24792-0303-4d5f-86de-c3b2a19fc74e.filletArc"),sQuery(id+"F0.wireOp",EDGE,"5ffe84d5-8cdf-4c2e-9e98-3655a6b86056.filletArc"),sQuery(id+"F0.wireOp",EDGE,"e8945d06-678d-4789-81f5-b1335d2624b7.filletArc"),sQuery(id+"F0.wireOp",EDGE,"a0b45458-2819-4e46-80a9-56e3c7e3f3b4.trimOffspring"),sQuery(id+"F0.wireOp",EDGE,"bf295548-413a-4249-b2ed-de7f7c0a0b82"),sQuery(id+"F0.wireOp",EDGE,"b03dbe81-5cdf-4ba7-a8f7-bb7ec46ab3a8"),sQuery(id+"F0.wireOp",EDGE,"b0d05724-446d-4885-847a-915c569f1139"),sQuery(id+"F0.wireOp",EDGE,"608d76ae-a745-4fd0-ae95-f5732494cd55.filletArc"),sQuery(id+"F0.wireOp",EDGE,"a41367dd-7dbd-4f08-888b-74168a8e5936.filletArc"),sQuery(id+"F0.wireOp",EDGE,"84e31002-7089-4eef-81a0-79c8965d61ed.filletArc"),sQuery(id+"F0.wireOp",EDGE,"1335fa2d-2410-4889-a90b-ae026db059b2.trimOffspring"),sQuery(id+"F0.wireOp",EDGE,"81157b49-ae94-446f-8b4e-5ce1e116e724.trimOffspring"),sQuery(id+"F0.wireOp",EDGE,"4f1c551e-3bfd-48a9-873a-6291d27f8455.trimOffspring"),sQuery(id+"F0.wireOp",EDGE,"E13.filletArc"),sQuery(id+"F0.wireOp",EDGE,"E14.filletArc"),sQuery(id+"F0.wireOp",EDGE,"E15.filletArc"),sQuery(id+"F0.wireOp",EDGE,"E16.filletArc"),sQuery(id+"F0.wireOp",EDGE,"E17.filletArc"),sQuery(id+"F0.wireOp",EDGE,"E18.filletArc")])],"isStart":true});
            var sketch = newSketch(context, id + "F16", { "sketchPlane" : qUnion([Q0])});
            skLineSegment(sketch, "E56", {"start": v(80.17, 27.6) * mm, "end": v(80.17, 22.38) * mm});
            skArc(sketch, "E57", {"start": v(80.17, 32.84) * mm, "mid": v(74.94, 27.6) * mm, "end": v(80.17, 22.38) * mm});
            skLineSegment(sketch, "E58", {"start": v(80.17, 27.6) * mm, "end": v(80.17, 32.84) * mm});
            skSolve(sketch);
        }
        {
            var Q0;
            {var subQ0=sQuery(id+"F5.wireOp",EDGE,"E40");Q0=makeQuery(id+"F5.imprint","IMPRINT",FACE,{"disambiguationData":[TD([[makeQuery(id+"F5.imprint","IMPRINT",EDGE,{"derivedFrom":subQ0}),1.0]])]});}
            var Q1;
            {var subQ0=sQuery(id+"F5.wireOp",EDGE,"E39");var subQ1=sQuery(id+"F5.wireOp",EDGE,"E38");var subQ2=makeQuery(id+"F5.imprint","INTERSECT",VERTEX,{"derivedFrom":[subQ1,subQ0]});Q1=makeQuery(id+"F5.imprint","IMPRINT",FACE,{"disambiguationData":[TD([[makeQuery(id+"F5.imprint","IMPRINT",EDGE,{"disambiguationData":[TD([[subQ2,-1.0]])],"derivedFrom":subQ1}),-1.0]])]});}
            var Q2;
            Q2=sQuery(id+"F5.wireOp",EDGE,"E39");
            revolve(context, id + "F17", {"surfaceOperationType" : NewSurfaceOperationType.NEW, "entities" : qUnion([Q0, Q1]), "axis" : qUnion([Q2]), "revolveType" : RevolveType.FULL});
        }
        {
            var Q0;
            {var subQ0=sQuery(id+"F16.wireOp",EDGE,"E57");Q0=makeQuery(id+"F16.imprint","IMPRINT",FACE,{"disambiguationData":[TD([[makeQuery(id+"F16.imprint","IMPRINT",EDGE,{"derivedFrom":subQ0}),1.0]])]});}
            var Q1;
            {var subQ0=sQuery(id+"F16.wireOp",EDGE,"E58");var subQ1=sQuery(id+"F16.wireOp",EDGE,"E56");var subQ2=makeQuery(id+"F16.imprint","INTERSECT",VERTEX,{"derivedFrom":[subQ1,subQ0]});Q1=makeQuery(id+"F16.imprint","IMPRINT",FACE,{"disambiguationData":[TD([[makeQuery(id+"F16.imprint","IMPRINT",EDGE,{"disambiguationData":[TD([[subQ2,-1.0]])],"derivedFrom":subQ1}),-1.0]])]});}
            var Q2;
            Q2=sQuery(id+"F16.wireOp",EDGE,"E56");
            revolve(context, id + "F18", {"surfaceOperationType" : NewSurfaceOperationType.NEW, "entities" : qUnion([Q0, Q1]), "axis" : qUnion([Q2]), "revolveType" : RevolveType.FULL});
        }
        {
            var Q0;
            Q0=makeQuery(id+"F2.opExtrude","CAP_FACE",FACE,{"disambiguationData":[OSD([sQuery(id+"F0.wireOp",EDGE,"E0"),sQuery(id+"F0.wireOp",EDGE,"tXCEuyxa-6lNA-QPCA-4HXf-ApKYShcEb0Yf"),sQuery(id+"F0.wireOp",EDGE,"E1"),sQuery(id+"F0.wireOp",EDGE,"E2"),sQuery(id+"F0.wireOp",EDGE,"E3"),sQuery(id+"F0.wireOp",EDGE,"E4"),sQuery(id+"F0.wireOp",EDGE,"E5"),sQuery(id+"F0.wireOp",EDGE,"E6"),sQuery(id+"F0.wireOp",EDGE,"E7"),sQuery(id+"F0.wireOp",EDGE,"E8"),sQuery(id+"F0.wireOp",EDGE,"E9"),sQuery(id+"F0.wireOp",EDGE,"0kcF6Lq4-WqBE-dODE-wINV-nyZN5JArXVcS"),sQuery(id+"F0.wireOp",EDGE,"VSrMeVpB-pvXp-ETii-wjF9-Px2PqwZYQnOt"),sQuery(id+"F0.wireOp",EDGE,"OGzEMItw-FQCu-QhKJ-kTiP-AlfaDmg1CYfA"),sQuery(id+"F0.wireOp",EDGE,"E10.filletArc"),sQuery(id+"F0.wireOp",EDGE,"E11.filletArc"),sQuery(id+"F0.wireOp",EDGE,"E12.filletArc"),sQuery(id+"F0.wireOp",EDGE,"61869019-6ff7-477d-8c79-2028de4a396b.trimOffspring"),sQuery(id+"F0.wireOp",EDGE,"b39f1e7b-d492-47c6-a918-6e9c5b166b17"),sQuery(id+"F0.wireOp",EDGE,"9a7d06a7-665d-4e92-ad9d-959fca317462"),sQuery(id+"F0.wireOp",EDGE,"db31c51f-78d2-4091-9bd3-34a254103f45"),sQuery(id+"F0.wireOp",EDGE,"aaf24792-0303-4d5f-86de-c3b2a19fc74e.filletArc"),sQuery(id+"F0.wireOp",EDGE,"5ffe84d5-8cdf-4c2e-9e98-3655a6b86056.filletArc"),sQuery(id+"F0.wireOp",EDGE,"e8945d06-678d-4789-81f5-b1335d2624b7.filletArc"),sQuery(id+"F0.wireOp",EDGE,"a0b45458-2819-4e46-80a9-56e3c7e3f3b4.trimOffspring"),sQuery(id+"F0.wireOp",EDGE,"bf295548-413a-4249-b2ed-de7f7c0a0b82"),sQuery(id+"F0.wireOp",EDGE,"b03dbe81-5cdf-4ba7-a8f7-bb7ec46ab3a8"),sQuery(id+"F0.wireOp",EDGE,"b0d05724-446d-4885-847a-915c569f1139"),sQuery(id+"F0.wireOp",EDGE,"608d76ae-a745-4fd0-ae95-f5732494cd55.filletArc"),sQuery(id+"F0.wireOp",EDGE,"a41367dd-7dbd-4f08-888b-74168a8e5936.filletArc"),sQuery(id+"F0.wireOp",EDGE,"84e31002-7089-4eef-81a0-79c8965d61ed.filletArc"),sQuery(id+"F0.wireOp",EDGE,"1335fa2d-2410-4889-a90b-ae026db059b2.trimOffspring"),sQuery(id+"F0.wireOp",EDGE,"81157b49-ae94-446f-8b4e-5ce1e116e724.trimOffspring"),sQuery(id+"F0.wireOp",EDGE,"4f1c551e-3bfd-48a9-873a-6291d27f8455.trimOffspring"),sQuery(id+"F0.wireOp",EDGE,"E13.filletArc"),sQuery(id+"F0.wireOp",EDGE,"E14.filletArc"),sQuery(id+"F0.wireOp",EDGE,"E15.filletArc"),sQuery(id+"F0.wireOp",EDGE,"E16.filletArc"),sQuery(id+"F0.wireOp",EDGE,"E17.filletArc"),sQuery(id+"F0.wireOp",EDGE,"E18.filletArc")])],"isStart":true});
            var sketch = newSketch(context, id + "F19", { "sketchPlane" : qUnion([Q0])});
            skLineSegment(sketch, "E59", {"start": v(46.4, -6.9) * mm, "end": v(46.4, -12.12) * mm});
            skArc(sketch, "E60", {"start": v(46.4, -1.66) * mm, "mid": v(41.17, -6.9) * mm, "end": v(46.4, -12.12) * mm});
            skLineSegment(sketch, "E61", {"start": v(46.4, -6.9) * mm, "end": v(46.4, -1.66) * mm});
            skSolve(sketch);
        }
        {
            var Q0;
            Q0 = qSketchRegion(id + "F19", true);
            var Q1;
            Q1=sQuery(id+"F19.wireOp",EDGE,"E59");
            revolve(context, id + "F20", {"surfaceOperationType" : NewSurfaceOperationType.NEW, "entities" : qUnion([Q0]), "axis" : qUnion([Q1]), "revolveType" : RevolveType.FULL});
        }
        {
            var Q0;
            Q0=makeQuery(id+"F15.opRevolve","SWEPT_BODY",BODY,{"disambiguationData":[OSD([sQuery(id+"F14.wireOp",EDGE,"E53"),sQuery(id+"F14.wireOp",EDGE,"E54"),sQuery(id+"F14.wireOp",EDGE,"E55")])]});
            var Q1;
            Q1=makeQuery(id+"F18.opRevolve","SWEPT_BODY",BODY,{"disambiguationData":[OSD([sQuery(id+"F16.wireOp",EDGE,"E56"),sQuery(id+"F16.wireOp",EDGE,"E57"),sQuery(id+"F16.wireOp",EDGE,"E58")])]});
            var Q2;
            Q2=makeQuery(id+"F13.opRevolve","SWEPT_BODY",BODY,{"disambiguationData":[OSD([sQuery(id+"F12.wireOp",EDGE,"E50"),sQuery(id+"F12.wireOp",EDGE,"E51"),sQuery(id+"F12.wireOp",EDGE,"E52")])]});
            var Q3;
            Q3=makeQuery(id+"F9.opRevolve","SWEPT_BODY",BODY,{"disambiguationData":[OSD([sQuery(id+"F8.wireOp",EDGE,"E44"),sQuery(id+"F8.wireOp",EDGE,"E45"),sQuery(id+"F8.wireOp",EDGE,"E46")])]});
            var Q4;
            Q4=makeQuery(id+"F11.opRevolve","SWEPT_BODY",BODY,{"disambiguationData":[OSD([sQuery(id+"F10.wireOp",EDGE,"E47"),sQuery(id+"F10.wireOp",EDGE,"E48"),sQuery(id+"F10.wireOp",EDGE,"E49")])]});
            var Q5;
            Q5=makeQuery(id+"F20.opRevolve","SWEPT_BODY",BODY,{"disambiguationData":[OSD([sQuery(id+"F19.wireOp",EDGE,"E59"),sQuery(id+"F19.wireOp",EDGE,"E60"),sQuery(id+"F19.wireOp",EDGE,"E61")])]});
            var Q6;
            Q6=makeQuery(id+"F17.opRevolve","SWEPT_BODY",BODY,{"disambiguationData":[OSD([sQuery(id+"F5.wireOp",EDGE,"E38"),sQuery(id+"F5.wireOp",EDGE,"E39"),sQuery(id+"F5.wireOp",EDGE,"E40")])]});
            var Q7;
            Q7=makeQuery(id+"F4.opRevolve","SWEPT_BODY",BODY,{"disambiguationData":[OSD([sQuery(id+"F3.wireOp",EDGE,"E35"),sQuery(id+"F3.wireOp",EDGE,"E36"),sQuery(id+"F3.wireOp",EDGE,"E37")])]});
            var Q8;
            Q8=makeQuery(id+"F7.opRevolve","SWEPT_BODY",BODY,{"disambiguationData":[OSD([sQuery(id+"F6.wireOp",EDGE,"E41"),sQuery(id+"F6.wireOp",EDGE,"E42"),sQuery(id+"F6.wireOp",EDGE,"E43")])]});
            var Q9;
            Q9=makeQuery(id+"F1.opExtrude","SWEPT_BODY",BODY,{"disambiguationData":[OSD([sQuery(id+"F0.wireOp",EDGE,"E0"),sQuery(id+"F0.wireOp",EDGE,"tXCEuyxa-6lNA-QPCA-4HXf-ApKYShcEb0Yf"),sQuery(id+"F0.wireOp",EDGE,"E1"),sQuery(id+"F0.wireOp",EDGE,"E2"),sQuery(id+"F0.wireOp",EDGE,"E3"),sQuery(id+"F0.wireOp",EDGE,"E4"),sQuery(id+"F0.wireOp",EDGE,"E5"),sQuery(id+"F0.wireOp",EDGE,"E6"),sQuery(id+"F0.wireOp",EDGE,"E7"),sQuery(id+"F0.wireOp",EDGE,"E8"),sQuery(id+"F0.wireOp",EDGE,"E9"),sQuery(id+"F0.wireOp",EDGE,"0kcF6Lq4-WqBE-dODE-wINV-nyZN5JArXVcS"),sQuery(id+"F0.wireOp",EDGE,"VSrMeVpB-pvXp-ETii-wjF9-Px2PqwZYQnOt"),sQuery(id+"F0.wireOp",EDGE,"OGzEMItw-FQCu-QhKJ-kTiP-AlfaDmg1CYfA"),sQuery(id+"F0.wireOp",EDGE,"E10.filletArc"),sQuery(id+"F0.wireOp",EDGE,"E11.filletArc"),sQuery(id+"F0.wireOp",EDGE,"E12.filletArc"),sQuery(id+"F0.wireOp",EDGE,"61869019-6ff7-477d-8c79-2028de4a396b.trimOffspring"),sQuery(id+"F0.wireOp",EDGE,"b39f1e7b-d492-47c6-a918-6e9c5b166b17"),sQuery(id+"F0.wireOp",EDGE,"9a7d06a7-665d-4e92-ad9d-959fca317462"),sQuery(id+"F0.wireOp",EDGE,"db31c51f-78d2-4091-9bd3-34a254103f45"),sQuery(id+"F0.wireOp",EDGE,"aaf24792-0303-4d5f-86de-c3b2a19fc74e.filletArc"),sQuery(id+"F0.wireOp",EDGE,"5ffe84d5-8cdf-4c2e-9e98-3655a6b86056.filletArc"),sQuery(id+"F0.wireOp",EDGE,"e8945d06-678d-4789-81f5-b1335d2624b7.filletArc"),sQuery(id+"F0.wireOp",EDGE,"a0b45458-2819-4e46-80a9-56e3c7e3f3b4.trimOffspring"),sQuery(id+"F0.wireOp",EDGE,"bf295548-413a-4249-b2ed-de7f7c0a0b82"),sQuery(id+"F0.wireOp",EDGE,"b03dbe81-5cdf-4ba7-a8f7-bb7ec46ab3a8"),sQuery(id+"F0.wireOp",EDGE,"b0d05724-446d-4885-847a-915c569f1139"),sQuery(id+"F0.wireOp",EDGE,"608d76ae-a745-4fd0-ae95-f5732494cd55.filletArc"),sQuery(id+"F0.wireOp",EDGE,"a41367dd-7dbd-4f08-888b-74168a8e5936.filletArc"),sQuery(id+"F0.wireOp",EDGE,"84e31002-7089-4eef-81a0-79c8965d61ed.filletArc"),sQuery(id+"F0.wireOp",EDGE,"1335fa2d-2410-4889-a90b-ae026db059b2.trimOffspring"),sQuery(id+"F0.wireOp",EDGE,"81157b49-ae94-446f-8b4e-5ce1e116e724.trimOffspring"),sQuery(id+"F0.wireOp",EDGE,"4f1c551e-3bfd-48a9-873a-6291d27f8455.trimOffspring"),sQuery(id+"F0.wireOp",EDGE,"E13.filletArc"),sQuery(id+"F0.wireOp",EDGE,"E14.filletArc"),sQuery(id+"F0.wireOp",EDGE,"E15.filletArc"),sQuery(id+"F0.wireOp",EDGE,"E16.filletArc"),sQuery(id+"F0.wireOp",EDGE,"E17.filletArc"),sQuery(id+"F0.wireOp",EDGE,"E18.filletArc")])]});
            var Q10;
            Q10=makeQuery(id+"F2.opExtrude","SWEPT_BODY",BODY,{"disambiguationData":[OSD([sQuery(id+"F0.wireOp",EDGE,"E0"),sQuery(id+"F0.wireOp",EDGE,"tXCEuyxa-6lNA-QPCA-4HXf-ApKYShcEb0Yf"),sQuery(id+"F0.wireOp",EDGE,"E1"),sQuery(id+"F0.wireOp",EDGE,"E2"),sQuery(id+"F0.wireOp",EDGE,"E3"),sQuery(id+"F0.wireOp",EDGE,"E4"),sQuery(id+"F0.wireOp",EDGE,"E5"),sQuery(id+"F0.wireOp",EDGE,"E6"),sQuery(id+"F0.wireOp",EDGE,"E7"),sQuery(id+"F0.wireOp",EDGE,"E8"),sQuery(id+"F0.wireOp",EDGE,"E9"),sQuery(id+"F0.wireOp",EDGE,"0kcF6Lq4-WqBE-dODE-wINV-nyZN5JArXVcS"),sQuery(id+"F0.wireOp",EDGE,"VSrMeVpB-pvXp-ETii-wjF9-Px2PqwZYQnOt"),sQuery(id+"F0.wireOp",EDGE,"OGzEMItw-FQCu-QhKJ-kTiP-AlfaDmg1CYfA"),sQuery(id+"F0.wireOp",EDGE,"E10.filletArc"),sQuery(id+"F0.wireOp",EDGE,"E11.filletArc"),sQuery(id+"F0.wireOp",EDGE,"E12.filletArc"),sQuery(id+"F0.wireOp",EDGE,"61869019-6ff7-477d-8c79-2028de4a396b.trimOffspring"),sQuery(id+"F0.wireOp",EDGE,"b39f1e7b-d492-47c6-a918-6e9c5b166b17"),sQuery(id+"F0.wireOp",EDGE,"9a7d06a7-665d-4e92-ad9d-959fca317462"),sQuery(id+"F0.wireOp",EDGE,"db31c51f-78d2-4091-9bd3-34a254103f45"),sQuery(id+"F0.wireOp",EDGE,"aaf24792-0303-4d5f-86de-c3b2a19fc74e.filletArc"),sQuery(id+"F0.wireOp",EDGE,"5ffe84d5-8cdf-4c2e-9e98-3655a6b86056.filletArc"),sQuery(id+"F0.wireOp",EDGE,"e8945d06-678d-4789-81f5-b1335d2624b7.filletArc"),sQuery(id+"F0.wireOp",EDGE,"a0b45458-2819-4e46-80a9-56e3c7e3f3b4.trimOffspring"),sQuery(id+"F0.wireOp",EDGE,"bf295548-413a-4249-b2ed-de7f7c0a0b82"),sQuery(id+"F0.wireOp",EDGE,"b03dbe81-5cdf-4ba7-a8f7-bb7ec46ab3a8"),sQuery(id+"F0.wireOp",EDGE,"b0d05724-446d-4885-847a-915c569f1139"),sQuery(id+"F0.wireOp",EDGE,"608d76ae-a745-4fd0-ae95-f5732494cd55.filletArc"),sQuery(id+"F0.wireOp",EDGE,"a41367dd-7dbd-4f08-888b-74168a8e5936.filletArc"),sQuery(id+"F0.wireOp",EDGE,"84e31002-7089-4eef-81a0-79c8965d61ed.filletArc"),sQuery(id+"F0.wireOp",EDGE,"1335fa2d-2410-4889-a90b-ae026db059b2.trimOffspring"),sQuery(id+"F0.wireOp",EDGE,"81157b49-ae94-446f-8b4e-5ce1e116e724.trimOffspring"),sQuery(id+"F0.wireOp",EDGE,"4f1c551e-3bfd-48a9-873a-6291d27f8455.trimOffspring"),sQuery(id+"F0.wireOp",EDGE,"E13.filletArc"),sQuery(id+"F0.wireOp",EDGE,"E14.filletArc"),sQuery(id+"F0.wireOp",EDGE,"E15.filletArc"),sQuery(id+"F0.wireOp",EDGE,"E16.filletArc"),sQuery(id+"F0.wireOp",EDGE,"E17.filletArc"),sQuery(id+"F0.wireOp",EDGE,"E18.filletArc")])]});
            booleanBodies(context, id + "F21", {"operationType" : BooleanOperationType.SUBTRACTION, "tools" : qUnion([Q0, Q1, Q2, Q3, Q4, Q5, Q6, Q7, Q8]), "targets" : qUnion([Q9, Q10])});
        }
        {
            var Q0;
            Q0=makeQuery(id+"F2.opExtrude","CAP_FACE",FACE,{"disambiguationData":[OSD([sQuery(id+"F0.wireOp",EDGE,"E0"),sQuery(id+"F0.wireOp",EDGE,"tXCEuyxa-6lNA-QPCA-4HXf-ApKYShcEb0Yf"),sQuery(id+"F0.wireOp",EDGE,"E1"),sQuery(id+"F0.wireOp",EDGE,"E2"),sQuery(id+"F0.wireOp",EDGE,"E3"),sQuery(id+"F0.wireOp",EDGE,"E4"),sQuery(id+"F0.wireOp",EDGE,"E5"),sQuery(id+"F0.wireOp",EDGE,"E6"),sQuery(id+"F0.wireOp",EDGE,"E7"),sQuery(id+"F0.wireOp",EDGE,"E8"),sQuery(id+"F0.wireOp",EDGE,"E9"),sQuery(id+"F0.wireOp",EDGE,"0kcF6Lq4-WqBE-dODE-wINV-nyZN5JArXVcS"),sQuery(id+"F0.wireOp",EDGE,"VSrMeVpB-pvXp-ETii-wjF9-Px2PqwZYQnOt"),sQuery(id+"F0.wireOp",EDGE,"OGzEMItw-FQCu-QhKJ-kTiP-AlfaDmg1CYfA"),sQuery(id+"F0.wireOp",EDGE,"E10.filletArc"),sQuery(id+"F0.wireOp",EDGE,"E11.filletArc"),sQuery(id+"F0.wireOp",EDGE,"E12.filletArc"),sQuery(id+"F0.wireOp",EDGE,"61869019-6ff7-477d-8c79-2028de4a396b.trimOffspring"),sQuery(id+"F0.wireOp",EDGE,"b39f1e7b-d492-47c6-a918-6e9c5b166b17"),sQuery(id+"F0.wireOp",EDGE,"9a7d06a7-665d-4e92-ad9d-959fca317462"),sQuery(id+"F0.wireOp",EDGE,"db31c51f-78d2-4091-9bd3-34a254103f45"),sQuery(id+"F0.wireOp",EDGE,"aaf24792-0303-4d5f-86de-c3b2a19fc74e.filletArc"),sQuery(id+"F0.wireOp",EDGE,"5ffe84d5-8cdf-4c2e-9e98-3655a6b86056.filletArc"),sQuery(id+"F0.wireOp",EDGE,"e8945d06-678d-4789-81f5-b1335d2624b7.filletArc"),sQuery(id+"F0.wireOp",EDGE,"a0b45458-2819-4e46-80a9-56e3c7e3f3b4.trimOffspring"),sQuery(id+"F0.wireOp",EDGE,"bf295548-413a-4249-b2ed-de7f7c0a0b82"),sQuery(id+"F0.wireOp",EDGE,"b03dbe81-5cdf-4ba7-a8f7-bb7ec46ab3a8"),sQuery(id+"F0.wireOp",EDGE,"b0d05724-446d-4885-847a-915c569f1139"),sQuery(id+"F0.wireOp",EDGE,"608d76ae-a745-4fd0-ae95-f5732494cd55.filletArc"),sQuery(id+"F0.wireOp",EDGE,"a41367dd-7dbd-4f08-888b-74168a8e5936.filletArc"),sQuery(id+"F0.wireOp",EDGE,"84e31002-7089-4eef-81a0-79c8965d61ed.filletArc"),sQuery(id+"F0.wireOp",EDGE,"1335fa2d-2410-4889-a90b-ae026db059b2.trimOffspring"),sQuery(id+"F0.wireOp",EDGE,"81157b49-ae94-446f-8b4e-5ce1e116e724.trimOffspring"),sQuery(id+"F0.wireOp",EDGE,"4f1c551e-3bfd-48a9-873a-6291d27f8455.trimOffspring"),sQuery(id+"F0.wireOp",EDGE,"E13.filletArc"),sQuery(id+"F0.wireOp",EDGE,"E14.filletArc"),sQuery(id+"F0.wireOp",EDGE,"E15.filletArc"),sQuery(id+"F0.wireOp",EDGE,"E16.filletArc"),sQuery(id+"F0.wireOp",EDGE,"E17.filletArc"),sQuery(id+"F0.wireOp",EDGE,"E18.filletArc")])],"isStart":false});
            var sketch = newSketch(context, id + "F22", { "sketchPlane" : qUnion([Q0])});
            skCircle(sketch, "E62", {"center": v(73.24, -0.6) * mm, "radius": 5.39 * mm});
            skSolve(sketch);
        }
        {
            var Q0;
            Q0=makeQuery(id+"F22.imprint","IMPRINT",FACE,{"disambiguationData":[TD([[makeQuery(id+"F22.imprint","IMPRINT",EDGE,{"derivedFrom":sQuery(id+"F22.wireOp",EDGE,"E62")}),-1.0]])]});
            extrude(context, id + "F23", {"entities" : qUnion([Q0]), "oppositeDirection" : true, "depth" : 1 * mm, "offsetDistance" : 25 * mm});
        }
        {
            var Q0;
            Q0=makeQuery(id+"F1.opExtrude","CAP_EDGE",EDGE,{"disambiguationData":[OSD([sQuery(id+"F0.wireOp",EDGE,"E19.14")])],"isStart":false});
            var Q1;
            Q1=makeQuery(id+"F2.opExtrude","CAP_EDGE",EDGE,{"disambiguationData":[OSD([sQuery(id+"F0.wireOp",EDGE,"E19.14")])],"isStart":false});
            fillet(context, id + "F24", {"entities" : qUnion([Q0, Q1]), "radius" : 1.7 * mm, "tangentPropagation" : true, "allowEdgeOverflow" : false});
        }
        {
            var Q0;
            Q0=makeQuery(id+"F1.opExtrude","CAP_EDGE",EDGE,{"disambiguationData":[OSD([sQuery(id+"F0.wireOp",EDGE,"E0")])],"isStart":false});
            fillet(context, id + "F25", {"entities" : qUnion([Q0]), "radius" : .6 * mm, "tangentPropagation" : true, "allowEdgeOverflow" : false});
        }
        {
            var Q0;
            Q0=makeQuery(id+"F21.opBoolean","INTERSECT",EDGE,{"derivedFrom":[makeQuery(id+"F1.opExtrude","CAP_FACE",FACE,{"disambiguationData":[OSD([sQuery(id+"F0.wireOp",EDGE,"E0"),sQuery(id+"F0.wireOp",EDGE,"E1"),sQuery(id+"F0.wireOp",EDGE,"E2"),sQuery(id+"F0.wireOp",EDGE,"E3"),sQuery(id+"F0.wireOp",EDGE,"E4"),sQuery(id+"F0.wireOp",EDGE,"E5"),sQuery(id+"F0.wireOp",EDGE,"E6"),sQuery(id+"F0.wireOp",EDGE,"E7"),sQuery(id+"F0.wireOp",EDGE,"E8"),sQuery(id+"F0.wireOp",EDGE,"E9"),sQuery(id+"F0.wireOp",EDGE,"E19.0"),sQuery(id+"F0.wireOp",EDGE,"E19.1"),sQuery(id+"F0.wireOp",EDGE,"E19.2"),sQuery(id+"F0.wireOp",EDGE,"E19.3"),sQuery(id+"F0.wireOp",EDGE,"E19.4"),sQuery(id+"F0.wireOp",EDGE,"E19.5"),sQuery(id+"F0.wireOp",EDGE,"E19.6"),sQuery(id+"F0.wireOp",EDGE,"E19.7"),sQuery(id+"F0.wireOp",EDGE,"E19.8"),sQuery(id+"F0.wireOp",EDGE,"E19.9"),sQuery(id+"F0.wireOp",EDGE,"E19.10"),sQuery(id+"F0.wireOp",EDGE,"E19.11"),sQuery(id+"F0.wireOp",EDGE,"E19.12"),sQuery(id+"F0.wireOp",EDGE,"E19.13"),sQuery(id+"F0.wireOp",EDGE,"E19.14"),sQuery(id+"F0.wireOp",EDGE,"E20.0"),sQuery(id+"F0.wireOp",EDGE,"E21.0"),sQuery(id+"F0.wireOp",EDGE,"E22.0"),sQuery(id+"F0.wireOp",EDGE,"E23.0"),sQuery(id+"F0.wireOp",EDGE,"E24.0"),sQuery(id+"F0.wireOp",EDGE,"E25.0"),sQuery(id+"F0.wireOp",EDGE,"E26.0"),sQuery(id+"F0.wireOp",EDGE,"E27.0"),sQuery(id+"F0.wireOp",EDGE,"E28.0"),sQuery(id+"F0.wireOp",EDGE,"E29.0"),sQuery(id+"F0.wireOp",EDGE,"E30.0"),sQuery(id+"F0.wireOp",EDGE,"E31.0"),sQuery(id+"F0.wireOp",EDGE,"E32.0"),sQuery(id+"F0.wireOp",EDGE,"E33.0"),sQuery(id+"F0.wireOp",EDGE,"E34.0")])],"isStart":false}),makeQuery(id+"F7.opRevolve","SWEPT_FACE",FACE,{"disambiguationData":[OSD([sQuery(id+"F6.wireOp",EDGE,"E42")])]})]});
            var Q1;
            Q1=makeQuery(id+"F21.opBoolean","INTERSECT",EDGE,{"derivedFrom":[makeQuery(id+"F1.opExtrude","CAP_FACE",FACE,{"disambiguationData":[OSD([sQuery(id+"F0.wireOp",EDGE,"E0"),sQuery(id+"F0.wireOp",EDGE,"E1"),sQuery(id+"F0.wireOp",EDGE,"E2"),sQuery(id+"F0.wireOp",EDGE,"E3"),sQuery(id+"F0.wireOp",EDGE,"E4"),sQuery(id+"F0.wireOp",EDGE,"E5"),sQuery(id+"F0.wireOp",EDGE,"E6"),sQuery(id+"F0.wireOp",EDGE,"E7"),sQuery(id+"F0.wireOp",EDGE,"E8"),sQuery(id+"F0.wireOp",EDGE,"E9"),sQuery(id+"F0.wireOp",EDGE,"E19.0"),sQuery(id+"F0.wireOp",EDGE,"E19.1"),sQuery(id+"F0.wireOp",EDGE,"E19.2"),sQuery(id+"F0.wireOp",EDGE,"E19.3"),sQuery(id+"F0.wireOp",EDGE,"E19.4"),sQuery(id+"F0.wireOp",EDGE,"E19.5"),sQuery(id+"F0.wireOp",EDGE,"E19.6"),sQuery(id+"F0.wireOp",EDGE,"E19.7"),sQuery(id+"F0.wireOp",EDGE,"E19.8"),sQuery(id+"F0.wireOp",EDGE,"E19.9"),sQuery(id+"F0.wireOp",EDGE,"E19.10"),sQuery(id+"F0.wireOp",EDGE,"E19.11"),sQuery(id+"F0.wireOp",EDGE,"E19.12"),sQuery(id+"F0.wireOp",EDGE,"E19.13"),sQuery(id+"F0.wireOp",EDGE,"E19.14"),sQuery(id+"F0.wireOp",EDGE,"E20.0"),sQuery(id+"F0.wireOp",EDGE,"E21.0"),sQuery(id+"F0.wireOp",EDGE,"E22.0"),sQuery(id+"F0.wireOp",EDGE,"E23.0"),sQuery(id+"F0.wireOp",EDGE,"E24.0"),sQuery(id+"F0.wireOp",EDGE,"E25.0"),sQuery(id+"F0.wireOp",EDGE,"E26.0"),sQuery(id+"F0.wireOp",EDGE,"E27.0"),sQuery(id+"F0.wireOp",EDGE,"E28.0"),sQuery(id+"F0.wireOp",EDGE,"E29.0"),sQuery(id+"F0.wireOp",EDGE,"E30.0"),sQuery(id+"F0.wireOp",EDGE,"E31.0"),sQuery(id+"F0.wireOp",EDGE,"E32.0"),sQuery(id+"F0.wireOp",EDGE,"E33.0"),sQuery(id+"F0.wireOp",EDGE,"E34.0")])],"isStart":false}),makeQuery(id+"F9.opRevolve","SWEPT_FACE",FACE,{"disambiguationData":[OSD([sQuery(id+"F8.wireOp",EDGE,"E45")])]})]});
            var Q2;
            Q2=makeQuery(id+"F21.opBoolean","INTERSECT",EDGE,{"derivedFrom":[makeQuery(id+"F1.opExtrude","CAP_FACE",FACE,{"disambiguationData":[OSD([sQuery(id+"F0.wireOp",EDGE,"E0"),sQuery(id+"F0.wireOp",EDGE,"E1"),sQuery(id+"F0.wireOp",EDGE,"E2"),sQuery(id+"F0.wireOp",EDGE,"E3"),sQuery(id+"F0.wireOp",EDGE,"E4"),sQuery(id+"F0.wireOp",EDGE,"E5"),sQuery(id+"F0.wireOp",EDGE,"E6"),sQuery(id+"F0.wireOp",EDGE,"E7"),sQuery(id+"F0.wireOp",EDGE,"E8"),sQuery(id+"F0.wireOp",EDGE,"E9"),sQuery(id+"F0.wireOp",EDGE,"E19.0"),sQuery(id+"F0.wireOp",EDGE,"E19.1"),sQuery(id+"F0.wireOp",EDGE,"E19.2"),sQuery(id+"F0.wireOp",EDGE,"E19.3"),sQuery(id+"F0.wireOp",EDGE,"E19.4"),sQuery(id+"F0.wireOp",EDGE,"E19.5"),sQuery(id+"F0.wireOp",EDGE,"E19.6"),sQuery(id+"F0.wireOp",EDGE,"E19.7"),sQuery(id+"F0.wireOp",EDGE,"E19.8"),sQuery(id+"F0.wireOp",EDGE,"E19.9"),sQuery(id+"F0.wireOp",EDGE,"E19.10"),sQuery(id+"F0.wireOp",EDGE,"E19.11"),sQuery(id+"F0.wireOp",EDGE,"E19.12"),sQuery(id+"F0.wireOp",EDGE,"E19.13"),sQuery(id+"F0.wireOp",EDGE,"E19.14"),sQuery(id+"F0.wireOp",EDGE,"E20.0"),sQuery(id+"F0.wireOp",EDGE,"E21.0"),sQuery(id+"F0.wireOp",EDGE,"E22.0"),sQuery(id+"F0.wireOp",EDGE,"E23.0"),sQuery(id+"F0.wireOp",EDGE,"E24.0"),sQuery(id+"F0.wireOp",EDGE,"E25.0"),sQuery(id+"F0.wireOp",EDGE,"E26.0"),sQuery(id+"F0.wireOp",EDGE,"E27.0"),sQuery(id+"F0.wireOp",EDGE,"E28.0"),sQuery(id+"F0.wireOp",EDGE,"E29.0"),sQuery(id+"F0.wireOp",EDGE,"E30.0"),sQuery(id+"F0.wireOp",EDGE,"E31.0"),sQuery(id+"F0.wireOp",EDGE,"E32.0"),sQuery(id+"F0.wireOp",EDGE,"E33.0"),sQuery(id+"F0.wireOp",EDGE,"E34.0")])],"isStart":false}),makeQuery(id+"F11.opRevolve","SWEPT_FACE",FACE,{"disambiguationData":[OSD([sQuery(id+"F10.wireOp",EDGE,"E48")])]})]});
            var Q3;
            Q3=makeQuery(id+"F21.opBoolean","INTERSECT",EDGE,{"derivedFrom":[makeQuery(id+"F1.opExtrude","CAP_FACE",FACE,{"disambiguationData":[OSD([sQuery(id+"F0.wireOp",EDGE,"E0"),sQuery(id+"F0.wireOp",EDGE,"E1"),sQuery(id+"F0.wireOp",EDGE,"E2"),sQuery(id+"F0.wireOp",EDGE,"E3"),sQuery(id+"F0.wireOp",EDGE,"E4"),sQuery(id+"F0.wireOp",EDGE,"E5"),sQuery(id+"F0.wireOp",EDGE,"E6"),sQuery(id+"F0.wireOp",EDGE,"E7"),sQuery(id+"F0.wireOp",EDGE,"E8"),sQuery(id+"F0.wireOp",EDGE,"E9"),sQuery(id+"F0.wireOp",EDGE,"E19.0"),sQuery(id+"F0.wireOp",EDGE,"E19.1"),sQuery(id+"F0.wireOp",EDGE,"E19.2"),sQuery(id+"F0.wireOp",EDGE,"E19.3"),sQuery(id+"F0.wireOp",EDGE,"E19.4"),sQuery(id+"F0.wireOp",EDGE,"E19.5"),sQuery(id+"F0.wireOp",EDGE,"E19.6"),sQuery(id+"F0.wireOp",EDGE,"E19.7"),sQuery(id+"F0.wireOp",EDGE,"E19.8"),sQuery(id+"F0.wireOp",EDGE,"E19.9"),sQuery(id+"F0.wireOp",EDGE,"E19.10"),sQuery(id+"F0.wireOp",EDGE,"E19.11"),sQuery(id+"F0.wireOp",EDGE,"E19.12"),sQuery(id+"F0.wireOp",EDGE,"E19.13"),sQuery(id+"F0.wireOp",EDGE,"E19.14"),sQuery(id+"F0.wireOp",EDGE,"E20.0"),sQuery(id+"F0.wireOp",EDGE,"E21.0"),sQuery(id+"F0.wireOp",EDGE,"E22.0"),sQuery(id+"F0.wireOp",EDGE,"E23.0"),sQuery(id+"F0.wireOp",EDGE,"E24.0"),sQuery(id+"F0.wireOp",EDGE,"E25.0"),sQuery(id+"F0.wireOp",EDGE,"E26.0"),sQuery(id+"F0.wireOp",EDGE,"E27.0"),sQuery(id+"F0.wireOp",EDGE,"E28.0"),sQuery(id+"F0.wireOp",EDGE,"E29.0"),sQuery(id+"F0.wireOp",EDGE,"E30.0"),sQuery(id+"F0.wireOp",EDGE,"E31.0"),sQuery(id+"F0.wireOp",EDGE,"E32.0"),sQuery(id+"F0.wireOp",EDGE,"E33.0"),sQuery(id+"F0.wireOp",EDGE,"E34.0")])],"isStart":false}),makeQuery(id+"F4.opRevolve","SWEPT_FACE",FACE,{"disambiguationData":[OSD([sQuery(id+"F3.wireOp",EDGE,"E37")])]})]});
            var Q4;
            Q4=makeQuery(id+"F21.opBoolean","INTERSECT",EDGE,{"derivedFrom":[makeQuery(id+"F1.opExtrude","CAP_FACE",FACE,{"disambiguationData":[OSD([sQuery(id+"F0.wireOp",EDGE,"E0"),sQuery(id+"F0.wireOp",EDGE,"E1"),sQuery(id+"F0.wireOp",EDGE,"E2"),sQuery(id+"F0.wireOp",EDGE,"E3"),sQuery(id+"F0.wireOp",EDGE,"E4"),sQuery(id+"F0.wireOp",EDGE,"E5"),sQuery(id+"F0.wireOp",EDGE,"E6"),sQuery(id+"F0.wireOp",EDGE,"E7"),sQuery(id+"F0.wireOp",EDGE,"E8"),sQuery(id+"F0.wireOp",EDGE,"E9"),sQuery(id+"F0.wireOp",EDGE,"E19.0"),sQuery(id+"F0.wireOp",EDGE,"E19.1"),sQuery(id+"F0.wireOp",EDGE,"E19.2"),sQuery(id+"F0.wireOp",EDGE,"E19.3"),sQuery(id+"F0.wireOp",EDGE,"E19.4"),sQuery(id+"F0.wireOp",EDGE,"E19.5"),sQuery(id+"F0.wireOp",EDGE,"E19.6"),sQuery(id+"F0.wireOp",EDGE,"E19.7"),sQuery(id+"F0.wireOp",EDGE,"E19.8"),sQuery(id+"F0.wireOp",EDGE,"E19.9"),sQuery(id+"F0.wireOp",EDGE,"E19.10"),sQuery(id+"F0.wireOp",EDGE,"E19.11"),sQuery(id+"F0.wireOp",EDGE,"E19.12"),sQuery(id+"F0.wireOp",EDGE,"E19.13"),sQuery(id+"F0.wireOp",EDGE,"E19.14"),sQuery(id+"F0.wireOp",EDGE,"E20.0"),sQuery(id+"F0.wireOp",EDGE,"E21.0"),sQuery(id+"F0.wireOp",EDGE,"E22.0"),sQuery(id+"F0.wireOp",EDGE,"E23.0"),sQuery(id+"F0.wireOp",EDGE,"E24.0"),sQuery(id+"F0.wireOp",EDGE,"E25.0"),sQuery(id+"F0.wireOp",EDGE,"E26.0"),sQuery(id+"F0.wireOp",EDGE,"E27.0"),sQuery(id+"F0.wireOp",EDGE,"E28.0"),sQuery(id+"F0.wireOp",EDGE,"E29.0"),sQuery(id+"F0.wireOp",EDGE,"E30.0"),sQuery(id+"F0.wireOp",EDGE,"E31.0"),sQuery(id+"F0.wireOp",EDGE,"E32.0"),sQuery(id+"F0.wireOp",EDGE,"E33.0"),sQuery(id+"F0.wireOp",EDGE,"E34.0")])],"isStart":false}),makeQuery(id+"F20.opRevolve","SWEPT_FACE",FACE,{"disambiguationData":[OSD([sQuery(id+"F19.wireOp",EDGE,"E60")])]})]});
            var Q5;
            Q5=makeQuery(id+"F21.opBoolean","INTERSECT",EDGE,{"derivedFrom":[makeQuery(id+"F1.opExtrude","CAP_FACE",FACE,{"disambiguationData":[OSD([sQuery(id+"F0.wireOp",EDGE,"E0"),sQuery(id+"F0.wireOp",EDGE,"E1"),sQuery(id+"F0.wireOp",EDGE,"E2"),sQuery(id+"F0.wireOp",EDGE,"E3"),sQuery(id+"F0.wireOp",EDGE,"E4"),sQuery(id+"F0.wireOp",EDGE,"E5"),sQuery(id+"F0.wireOp",EDGE,"E6"),sQuery(id+"F0.wireOp",EDGE,"E7"),sQuery(id+"F0.wireOp",EDGE,"E8"),sQuery(id+"F0.wireOp",EDGE,"E9"),sQuery(id+"F0.wireOp",EDGE,"E19.0"),sQuery(id+"F0.wireOp",EDGE,"E19.1"),sQuery(id+"F0.wireOp",EDGE,"E19.2"),sQuery(id+"F0.wireOp",EDGE,"E19.3"),sQuery(id+"F0.wireOp",EDGE,"E19.4"),sQuery(id+"F0.wireOp",EDGE,"E19.5"),sQuery(id+"F0.wireOp",EDGE,"E19.6"),sQuery(id+"F0.wireOp",EDGE,"E19.7"),sQuery(id+"F0.wireOp",EDGE,"E19.8"),sQuery(id+"F0.wireOp",EDGE,"E19.9"),sQuery(id+"F0.wireOp",EDGE,"E19.10"),sQuery(id+"F0.wireOp",EDGE,"E19.11"),sQuery(id+"F0.wireOp",EDGE,"E19.12"),sQuery(id+"F0.wireOp",EDGE,"E19.13"),sQuery(id+"F0.wireOp",EDGE,"E19.14"),sQuery(id+"F0.wireOp",EDGE,"E20.0"),sQuery(id+"F0.wireOp",EDGE,"E21.0"),sQuery(id+"F0.wireOp",EDGE,"E22.0"),sQuery(id+"F0.wireOp",EDGE,"E23.0"),sQuery(id+"F0.wireOp",EDGE,"E24.0"),sQuery(id+"F0.wireOp",EDGE,"E25.0"),sQuery(id+"F0.wireOp",EDGE,"E26.0"),sQuery(id+"F0.wireOp",EDGE,"E27.0"),sQuery(id+"F0.wireOp",EDGE,"E28.0"),sQuery(id+"F0.wireOp",EDGE,"E29.0"),sQuery(id+"F0.wireOp",EDGE,"E30.0"),sQuery(id+"F0.wireOp",EDGE,"E31.0"),sQuery(id+"F0.wireOp",EDGE,"E32.0"),sQuery(id+"F0.wireOp",EDGE,"E33.0"),sQuery(id+"F0.wireOp",EDGE,"E34.0")])],"isStart":false}),makeQuery(id+"F17.opRevolve","SWEPT_FACE",FACE,{"disambiguationData":[OSD([sQuery(id+"F5.wireOp",EDGE,"E40")])]})]});
            var Q6;
            Q6=makeQuery(id+"F21.opBoolean","INTERSECT",EDGE,{"derivedFrom":[makeQuery(id+"F1.opExtrude","CAP_FACE",FACE,{"disambiguationData":[OSD([sQuery(id+"F0.wireOp",EDGE,"E0"),sQuery(id+"F0.wireOp",EDGE,"E1"),sQuery(id+"F0.wireOp",EDGE,"E2"),sQuery(id+"F0.wireOp",EDGE,"E3"),sQuery(id+"F0.wireOp",EDGE,"E4"),sQuery(id+"F0.wireOp",EDGE,"E5"),sQuery(id+"F0.wireOp",EDGE,"E6"),sQuery(id+"F0.wireOp",EDGE,"E7"),sQuery(id+"F0.wireOp",EDGE,"E8"),sQuery(id+"F0.wireOp",EDGE,"E9"),sQuery(id+"F0.wireOp",EDGE,"E19.0"),sQuery(id+"F0.wireOp",EDGE,"E19.1"),sQuery(id+"F0.wireOp",EDGE,"E19.2"),sQuery(id+"F0.wireOp",EDGE,"E19.3"),sQuery(id+"F0.wireOp",EDGE,"E19.4"),sQuery(id+"F0.wireOp",EDGE,"E19.5"),sQuery(id+"F0.wireOp",EDGE,"E19.6"),sQuery(id+"F0.wireOp",EDGE,"E19.7"),sQuery(id+"F0.wireOp",EDGE,"E19.8"),sQuery(id+"F0.wireOp",EDGE,"E19.9"),sQuery(id+"F0.wireOp",EDGE,"E19.10"),sQuery(id+"F0.wireOp",EDGE,"E19.11"),sQuery(id+"F0.wireOp",EDGE,"E19.12"),sQuery(id+"F0.wireOp",EDGE,"E19.13"),sQuery(id+"F0.wireOp",EDGE,"E19.14"),sQuery(id+"F0.wireOp",EDGE,"E20.0"),sQuery(id+"F0.wireOp",EDGE,"E21.0"),sQuery(id+"F0.wireOp",EDGE,"E22.0"),sQuery(id+"F0.wireOp",EDGE,"E23.0"),sQuery(id+"F0.wireOp",EDGE,"E24.0"),sQuery(id+"F0.wireOp",EDGE,"E25.0"),sQuery(id+"F0.wireOp",EDGE,"E26.0"),sQuery(id+"F0.wireOp",EDGE,"E27.0"),sQuery(id+"F0.wireOp",EDGE,"E28.0"),sQuery(id+"F0.wireOp",EDGE,"E29.0"),sQuery(id+"F0.wireOp",EDGE,"E30.0"),sQuery(id+"F0.wireOp",EDGE,"E31.0"),sQuery(id+"F0.wireOp",EDGE,"E32.0"),sQuery(id+"F0.wireOp",EDGE,"E33.0"),sQuery(id+"F0.wireOp",EDGE,"E34.0")])],"isStart":false}),makeQuery(id+"F13.opRevolve","SWEPT_FACE",FACE,{"disambiguationData":[OSD([sQuery(id+"F12.wireOp",EDGE,"E51")])]})]});
            var Q7;
            Q7=makeQuery(id+"F21.opBoolean","INTERSECT",EDGE,{"derivedFrom":[makeQuery(id+"F1.opExtrude","CAP_FACE",FACE,{"disambiguationData":[OSD([sQuery(id+"F0.wireOp",EDGE,"E0"),sQuery(id+"F0.wireOp",EDGE,"E1"),sQuery(id+"F0.wireOp",EDGE,"E2"),sQuery(id+"F0.wireOp",EDGE,"E3"),sQuery(id+"F0.wireOp",EDGE,"E4"),sQuery(id+"F0.wireOp",EDGE,"E5"),sQuery(id+"F0.wireOp",EDGE,"E6"),sQuery(id+"F0.wireOp",EDGE,"E7"),sQuery(id+"F0.wireOp",EDGE,"E8"),sQuery(id+"F0.wireOp",EDGE,"E9"),sQuery(id+"F0.wireOp",EDGE,"E19.0"),sQuery(id+"F0.wireOp",EDGE,"E19.1"),sQuery(id+"F0.wireOp",EDGE,"E19.2"),sQuery(id+"F0.wireOp",EDGE,"E19.3"),sQuery(id+"F0.wireOp",EDGE,"E19.4"),sQuery(id+"F0.wireOp",EDGE,"E19.5"),sQuery(id+"F0.wireOp",EDGE,"E19.6"),sQuery(id+"F0.wireOp",EDGE,"E19.7"),sQuery(id+"F0.wireOp",EDGE,"E19.8"),sQuery(id+"F0.wireOp",EDGE,"E19.9"),sQuery(id+"F0.wireOp",EDGE,"E19.10"),sQuery(id+"F0.wireOp",EDGE,"E19.11"),sQuery(id+"F0.wireOp",EDGE,"E19.12"),sQuery(id+"F0.wireOp",EDGE,"E19.13"),sQuery(id+"F0.wireOp",EDGE,"E19.14"),sQuery(id+"F0.wireOp",EDGE,"E20.0"),sQuery(id+"F0.wireOp",EDGE,"E21.0"),sQuery(id+"F0.wireOp",EDGE,"E22.0"),sQuery(id+"F0.wireOp",EDGE,"E23.0"),sQuery(id+"F0.wireOp",EDGE,"E24.0"),sQuery(id+"F0.wireOp",EDGE,"E25.0"),sQuery(id+"F0.wireOp",EDGE,"E26.0"),sQuery(id+"F0.wireOp",EDGE,"E27.0"),sQuery(id+"F0.wireOp",EDGE,"E28.0"),sQuery(id+"F0.wireOp",EDGE,"E29.0"),sQuery(id+"F0.wireOp",EDGE,"E30.0"),sQuery(id+"F0.wireOp",EDGE,"E31.0"),sQuery(id+"F0.wireOp",EDGE,"E32.0"),sQuery(id+"F0.wireOp",EDGE,"E33.0"),sQuery(id+"F0.wireOp",EDGE,"E34.0")])],"isStart":false}),makeQuery(id+"F15.opRevolve","SWEPT_FACE",FACE,{"disambiguationData":[OSD([sQuery(id+"F14.wireOp",EDGE,"E54")])]})]});
            var Q8;
            Q8=makeQuery(id+"F21.opBoolean","INTERSECT",EDGE,{"derivedFrom":[makeQuery(id+"F1.opExtrude","CAP_FACE",FACE,{"disambiguationData":[OSD([sQuery(id+"F0.wireOp",EDGE,"E0"),sQuery(id+"F0.wireOp",EDGE,"E1"),sQuery(id+"F0.wireOp",EDGE,"E2"),sQuery(id+"F0.wireOp",EDGE,"E3"),sQuery(id+"F0.wireOp",EDGE,"E4"),sQuery(id+"F0.wireOp",EDGE,"E5"),sQuery(id+"F0.wireOp",EDGE,"E6"),sQuery(id+"F0.wireOp",EDGE,"E7"),sQuery(id+"F0.wireOp",EDGE,"E8"),sQuery(id+"F0.wireOp",EDGE,"E9"),sQuery(id+"F0.wireOp",EDGE,"E19.0"),sQuery(id+"F0.wireOp",EDGE,"E19.1"),sQuery(id+"F0.wireOp",EDGE,"E19.2"),sQuery(id+"F0.wireOp",EDGE,"E19.3"),sQuery(id+"F0.wireOp",EDGE,"E19.4"),sQuery(id+"F0.wireOp",EDGE,"E19.5"),sQuery(id+"F0.wireOp",EDGE,"E19.6"),sQuery(id+"F0.wireOp",EDGE,"E19.7"),sQuery(id+"F0.wireOp",EDGE,"E19.8"),sQuery(id+"F0.wireOp",EDGE,"E19.9"),sQuery(id+"F0.wireOp",EDGE,"E19.10"),sQuery(id+"F0.wireOp",EDGE,"E19.11"),sQuery(id+"F0.wireOp",EDGE,"E19.12"),sQuery(id+"F0.wireOp",EDGE,"E19.13"),sQuery(id+"F0.wireOp",EDGE,"E19.14"),sQuery(id+"F0.wireOp",EDGE,"E20.0"),sQuery(id+"F0.wireOp",EDGE,"E21.0"),sQuery(id+"F0.wireOp",EDGE,"E22.0"),sQuery(id+"F0.wireOp",EDGE,"E23.0"),sQuery(id+"F0.wireOp",EDGE,"E24.0"),sQuery(id+"F0.wireOp",EDGE,"E25.0"),sQuery(id+"F0.wireOp",EDGE,"E26.0"),sQuery(id+"F0.wireOp",EDGE,"E27.0"),sQuery(id+"F0.wireOp",EDGE,"E28.0"),sQuery(id+"F0.wireOp",EDGE,"E29.0"),sQuery(id+"F0.wireOp",EDGE,"E30.0"),sQuery(id+"F0.wireOp",EDGE,"E31.0"),sQuery(id+"F0.wireOp",EDGE,"E32.0"),sQuery(id+"F0.wireOp",EDGE,"E33.0"),sQuery(id+"F0.wireOp",EDGE,"E34.0")])],"isStart":false}),makeQuery(id+"F18.opRevolve","SWEPT_FACE",FACE,{"disambiguationData":[OSD([sQuery(id+"F16.wireOp",EDGE,"E57")])]})]});
            var Q9;
            Q9=makeQuery(id+"F21.opBoolean","INTERSECT",EDGE,{"derivedFrom":[makeQuery(id+"F2.opExtrude","CAP_FACE",FACE,{"disambiguationData":[OSD([sQuery(id+"F0.wireOp",EDGE,"E0"),sQuery(id+"F0.wireOp",EDGE,"E1"),sQuery(id+"F0.wireOp",EDGE,"E2"),sQuery(id+"F0.wireOp",EDGE,"E3"),sQuery(id+"F0.wireOp",EDGE,"E4"),sQuery(id+"F0.wireOp",EDGE,"E5"),sQuery(id+"F0.wireOp",EDGE,"E6"),sQuery(id+"F0.wireOp",EDGE,"E7"),sQuery(id+"F0.wireOp",EDGE,"E8"),sQuery(id+"F0.wireOp",EDGE,"E9"),sQuery(id+"F0.wireOp",EDGE,"E19.0"),sQuery(id+"F0.wireOp",EDGE,"E19.1"),sQuery(id+"F0.wireOp",EDGE,"E19.2"),sQuery(id+"F0.wireOp",EDGE,"E19.3"),sQuery(id+"F0.wireOp",EDGE,"E19.4"),sQuery(id+"F0.wireOp",EDGE,"E19.5"),sQuery(id+"F0.wireOp",EDGE,"E19.6"),sQuery(id+"F0.wireOp",EDGE,"E19.7"),sQuery(id+"F0.wireOp",EDGE,"E19.8"),sQuery(id+"F0.wireOp",EDGE,"E19.9"),sQuery(id+"F0.wireOp",EDGE,"E19.10"),sQuery(id+"F0.wireOp",EDGE,"E19.11"),sQuery(id+"F0.wireOp",EDGE,"E19.12"),sQuery(id+"F0.wireOp",EDGE,"E19.13"),sQuery(id+"F0.wireOp",EDGE,"E19.14"),sQuery(id+"F0.wireOp",EDGE,"E20.0"),sQuery(id+"F0.wireOp",EDGE,"E21.0"),sQuery(id+"F0.wireOp",EDGE,"E22.0"),sQuery(id+"F0.wireOp",EDGE,"E23.0"),sQuery(id+"F0.wireOp",EDGE,"E24.0"),sQuery(id+"F0.wireOp",EDGE,"E25.0"),sQuery(id+"F0.wireOp",EDGE,"E26.0"),sQuery(id+"F0.wireOp",EDGE,"E27.0"),sQuery(id+"F0.wireOp",EDGE,"E28.0"),sQuery(id+"F0.wireOp",EDGE,"E29.0"),sQuery(id+"F0.wireOp",EDGE,"E30.0"),sQuery(id+"F0.wireOp",EDGE,"E31.0"),sQuery(id+"F0.wireOp",EDGE,"E32.0"),sQuery(id+"F0.wireOp",EDGE,"E33.0"),sQuery(id+"F0.wireOp",EDGE,"E34.0")])],"isStart":false}),makeQuery(id+"F4.opRevolve","SWEPT_FACE",FACE,{"disambiguationData":[OSD([sQuery(id+"F3.wireOp",EDGE,"E37")])]})]});
            var Q10;
            Q10=makeQuery(id+"F21.opBoolean","INTERSECT",EDGE,{"derivedFrom":[makeQuery(id+"F2.opExtrude","CAP_FACE",FACE,{"disambiguationData":[OSD([sQuery(id+"F0.wireOp",EDGE,"E0"),sQuery(id+"F0.wireOp",EDGE,"E1"),sQuery(id+"F0.wireOp",EDGE,"E2"),sQuery(id+"F0.wireOp",EDGE,"E3"),sQuery(id+"F0.wireOp",EDGE,"E4"),sQuery(id+"F0.wireOp",EDGE,"E5"),sQuery(id+"F0.wireOp",EDGE,"E6"),sQuery(id+"F0.wireOp",EDGE,"E7"),sQuery(id+"F0.wireOp",EDGE,"E8"),sQuery(id+"F0.wireOp",EDGE,"E9"),sQuery(id+"F0.wireOp",EDGE,"E19.0"),sQuery(id+"F0.wireOp",EDGE,"E19.1"),sQuery(id+"F0.wireOp",EDGE,"E19.2"),sQuery(id+"F0.wireOp",EDGE,"E19.3"),sQuery(id+"F0.wireOp",EDGE,"E19.4"),sQuery(id+"F0.wireOp",EDGE,"E19.5"),sQuery(id+"F0.wireOp",EDGE,"E19.6"),sQuery(id+"F0.wireOp",EDGE,"E19.7"),sQuery(id+"F0.wireOp",EDGE,"E19.8"),sQuery(id+"F0.wireOp",EDGE,"E19.9"),sQuery(id+"F0.wireOp",EDGE,"E19.10"),sQuery(id+"F0.wireOp",EDGE,"E19.11"),sQuery(id+"F0.wireOp",EDGE,"E19.12"),sQuery(id+"F0.wireOp",EDGE,"E19.13"),sQuery(id+"F0.wireOp",EDGE,"E19.14"),sQuery(id+"F0.wireOp",EDGE,"E20.0"),sQuery(id+"F0.wireOp",EDGE,"E21.0"),sQuery(id+"F0.wireOp",EDGE,"E22.0"),sQuery(id+"F0.wireOp",EDGE,"E23.0"),sQuery(id+"F0.wireOp",EDGE,"E24.0"),sQuery(id+"F0.wireOp",EDGE,"E25.0"),sQuery(id+"F0.wireOp",EDGE,"E26.0"),sQuery(id+"F0.wireOp",EDGE,"E27.0"),sQuery(id+"F0.wireOp",EDGE,"E28.0"),sQuery(id+"F0.wireOp",EDGE,"E29.0"),sQuery(id+"F0.wireOp",EDGE,"E30.0"),sQuery(id+"F0.wireOp",EDGE,"E31.0"),sQuery(id+"F0.wireOp",EDGE,"E32.0"),sQuery(id+"F0.wireOp",EDGE,"E33.0"),sQuery(id+"F0.wireOp",EDGE,"E34.0")])],"isStart":false}),makeQuery(id+"F20.opRevolve","SWEPT_FACE",FACE,{"disambiguationData":[OSD([sQuery(id+"F19.wireOp",EDGE,"E60")])]})]});
            var Q11;
            Q11=makeQuery(id+"F21.opBoolean","INTERSECT",EDGE,{"derivedFrom":[makeQuery(id+"F2.opExtrude","CAP_FACE",FACE,{"disambiguationData":[OSD([sQuery(id+"F0.wireOp",EDGE,"E0"),sQuery(id+"F0.wireOp",EDGE,"E1"),sQuery(id+"F0.wireOp",EDGE,"E2"),sQuery(id+"F0.wireOp",EDGE,"E3"),sQuery(id+"F0.wireOp",EDGE,"E4"),sQuery(id+"F0.wireOp",EDGE,"E5"),sQuery(id+"F0.wireOp",EDGE,"E6"),sQuery(id+"F0.wireOp",EDGE,"E7"),sQuery(id+"F0.wireOp",EDGE,"E8"),sQuery(id+"F0.wireOp",EDGE,"E9"),sQuery(id+"F0.wireOp",EDGE,"E19.0"),sQuery(id+"F0.wireOp",EDGE,"E19.1"),sQuery(id+"F0.wireOp",EDGE,"E19.2"),sQuery(id+"F0.wireOp",EDGE,"E19.3"),sQuery(id+"F0.wireOp",EDGE,"E19.4"),sQuery(id+"F0.wireOp",EDGE,"E19.5"),sQuery(id+"F0.wireOp",EDGE,"E19.6"),sQuery(id+"F0.wireOp",EDGE,"E19.7"),sQuery(id+"F0.wireOp",EDGE,"E19.8"),sQuery(id+"F0.wireOp",EDGE,"E19.9"),sQuery(id+"F0.wireOp",EDGE,"E19.10"),sQuery(id+"F0.wireOp",EDGE,"E19.11"),sQuery(id+"F0.wireOp",EDGE,"E19.12"),sQuery(id+"F0.wireOp",EDGE,"E19.13"),sQuery(id+"F0.wireOp",EDGE,"E19.14"),sQuery(id+"F0.wireOp",EDGE,"E20.0"),sQuery(id+"F0.wireOp",EDGE,"E21.0"),sQuery(id+"F0.wireOp",EDGE,"E22.0"),sQuery(id+"F0.wireOp",EDGE,"E23.0"),sQuery(id+"F0.wireOp",EDGE,"E24.0"),sQuery(id+"F0.wireOp",EDGE,"E25.0"),sQuery(id+"F0.wireOp",EDGE,"E26.0"),sQuery(id+"F0.wireOp",EDGE,"E27.0"),sQuery(id+"F0.wireOp",EDGE,"E28.0"),sQuery(id+"F0.wireOp",EDGE,"E29.0"),sQuery(id+"F0.wireOp",EDGE,"E30.0"),sQuery(id+"F0.wireOp",EDGE,"E31.0"),sQuery(id+"F0.wireOp",EDGE,"E32.0"),sQuery(id+"F0.wireOp",EDGE,"E33.0"),sQuery(id+"F0.wireOp",EDGE,"E34.0")])],"isStart":false}),makeQuery(id+"F17.opRevolve","SWEPT_FACE",FACE,{"disambiguationData":[OSD([sQuery(id+"F5.wireOp",EDGE,"E40")])]})]});
            var Q12;
            Q12=makeQuery(id+"F21.opBoolean","INTERSECT",EDGE,{"derivedFrom":[makeQuery(id+"F2.opExtrude","CAP_FACE",FACE,{"disambiguationData":[OSD([sQuery(id+"F0.wireOp",EDGE,"E0"),sQuery(id+"F0.wireOp",EDGE,"E1"),sQuery(id+"F0.wireOp",EDGE,"E2"),sQuery(id+"F0.wireOp",EDGE,"E3"),sQuery(id+"F0.wireOp",EDGE,"E4"),sQuery(id+"F0.wireOp",EDGE,"E5"),sQuery(id+"F0.wireOp",EDGE,"E6"),sQuery(id+"F0.wireOp",EDGE,"E7"),sQuery(id+"F0.wireOp",EDGE,"E8"),sQuery(id+"F0.wireOp",EDGE,"E9"),sQuery(id+"F0.wireOp",EDGE,"E19.0"),sQuery(id+"F0.wireOp",EDGE,"E19.1"),sQuery(id+"F0.wireOp",EDGE,"E19.2"),sQuery(id+"F0.wireOp",EDGE,"E19.3"),sQuery(id+"F0.wireOp",EDGE,"E19.4"),sQuery(id+"F0.wireOp",EDGE,"E19.5"),sQuery(id+"F0.wireOp",EDGE,"E19.6"),sQuery(id+"F0.wireOp",EDGE,"E19.7"),sQuery(id+"F0.wireOp",EDGE,"E19.8"),sQuery(id+"F0.wireOp",EDGE,"E19.9"),sQuery(id+"F0.wireOp",EDGE,"E19.10"),sQuery(id+"F0.wireOp",EDGE,"E19.11"),sQuery(id+"F0.wireOp",EDGE,"E19.12"),sQuery(id+"F0.wireOp",EDGE,"E19.13"),sQuery(id+"F0.wireOp",EDGE,"E19.14"),sQuery(id+"F0.wireOp",EDGE,"E20.0"),sQuery(id+"F0.wireOp",EDGE,"E21.0"),sQuery(id+"F0.wireOp",EDGE,"E22.0"),sQuery(id+"F0.wireOp",EDGE,"E23.0"),sQuery(id+"F0.wireOp",EDGE,"E24.0"),sQuery(id+"F0.wireOp",EDGE,"E25.0"),sQuery(id+"F0.wireOp",EDGE,"E26.0"),sQuery(id+"F0.wireOp",EDGE,"E27.0"),sQuery(id+"F0.wireOp",EDGE,"E28.0"),sQuery(id+"F0.wireOp",EDGE,"E29.0"),sQuery(id+"F0.wireOp",EDGE,"E30.0"),sQuery(id+"F0.wireOp",EDGE,"E31.0"),sQuery(id+"F0.wireOp",EDGE,"E32.0"),sQuery(id+"F0.wireOp",EDGE,"E33.0"),sQuery(id+"F0.wireOp",EDGE,"E34.0")])],"isStart":false}),makeQuery(id+"F9.opRevolve","SWEPT_FACE",FACE,{"disambiguationData":[OSD([sQuery(id+"F8.wireOp",EDGE,"E45")])]})]});
            var Q13;
            Q13=makeQuery(id+"F21.opBoolean","INTERSECT",EDGE,{"derivedFrom":[makeQuery(id+"F2.opExtrude","CAP_FACE",FACE,{"disambiguationData":[OSD([sQuery(id+"F0.wireOp",EDGE,"E0"),sQuery(id+"F0.wireOp",EDGE,"E1"),sQuery(id+"F0.wireOp",EDGE,"E2"),sQuery(id+"F0.wireOp",EDGE,"E3"),sQuery(id+"F0.wireOp",EDGE,"E4"),sQuery(id+"F0.wireOp",EDGE,"E5"),sQuery(id+"F0.wireOp",EDGE,"E6"),sQuery(id+"F0.wireOp",EDGE,"E7"),sQuery(id+"F0.wireOp",EDGE,"E8"),sQuery(id+"F0.wireOp",EDGE,"E9"),sQuery(id+"F0.wireOp",EDGE,"E19.0"),sQuery(id+"F0.wireOp",EDGE,"E19.1"),sQuery(id+"F0.wireOp",EDGE,"E19.2"),sQuery(id+"F0.wireOp",EDGE,"E19.3"),sQuery(id+"F0.wireOp",EDGE,"E19.4"),sQuery(id+"F0.wireOp",EDGE,"E19.5"),sQuery(id+"F0.wireOp",EDGE,"E19.6"),sQuery(id+"F0.wireOp",EDGE,"E19.7"),sQuery(id+"F0.wireOp",EDGE,"E19.8"),sQuery(id+"F0.wireOp",EDGE,"E19.9"),sQuery(id+"F0.wireOp",EDGE,"E19.10"),sQuery(id+"F0.wireOp",EDGE,"E19.11"),sQuery(id+"F0.wireOp",EDGE,"E19.12"),sQuery(id+"F0.wireOp",EDGE,"E19.13"),sQuery(id+"F0.wireOp",EDGE,"E19.14"),sQuery(id+"F0.wireOp",EDGE,"E20.0"),sQuery(id+"F0.wireOp",EDGE,"E21.0"),sQuery(id+"F0.wireOp",EDGE,"E22.0"),sQuery(id+"F0.wireOp",EDGE,"E23.0"),sQuery(id+"F0.wireOp",EDGE,"E24.0"),sQuery(id+"F0.wireOp",EDGE,"E25.0"),sQuery(id+"F0.wireOp",EDGE,"E26.0"),sQuery(id+"F0.wireOp",EDGE,"E27.0"),sQuery(id+"F0.wireOp",EDGE,"E28.0"),sQuery(id+"F0.wireOp",EDGE,"E29.0"),sQuery(id+"F0.wireOp",EDGE,"E30.0"),sQuery(id+"F0.wireOp",EDGE,"E31.0"),sQuery(id+"F0.wireOp",EDGE,"E32.0"),sQuery(id+"F0.wireOp",EDGE,"E33.0"),sQuery(id+"F0.wireOp",EDGE,"E34.0")])],"isStart":false}),makeQuery(id+"F7.opRevolve","SWEPT_FACE",FACE,{"disambiguationData":[OSD([sQuery(id+"F6.wireOp",EDGE,"E42")])]})]});
            var Q14;
            Q14=makeQuery(id+"F21.opBoolean","INTERSECT",EDGE,{"derivedFrom":[makeQuery(id+"F2.opExtrude","CAP_FACE",FACE,{"disambiguationData":[OSD([sQuery(id+"F0.wireOp",EDGE,"E0"),sQuery(id+"F0.wireOp",EDGE,"E1"),sQuery(id+"F0.wireOp",EDGE,"E2"),sQuery(id+"F0.wireOp",EDGE,"E3"),sQuery(id+"F0.wireOp",EDGE,"E4"),sQuery(id+"F0.wireOp",EDGE,"E5"),sQuery(id+"F0.wireOp",EDGE,"E6"),sQuery(id+"F0.wireOp",EDGE,"E7"),sQuery(id+"F0.wireOp",EDGE,"E8"),sQuery(id+"F0.wireOp",EDGE,"E9"),sQuery(id+"F0.wireOp",EDGE,"E19.0"),sQuery(id+"F0.wireOp",EDGE,"E19.1"),sQuery(id+"F0.wireOp",EDGE,"E19.2"),sQuery(id+"F0.wireOp",EDGE,"E19.3"),sQuery(id+"F0.wireOp",EDGE,"E19.4"),sQuery(id+"F0.wireOp",EDGE,"E19.5"),sQuery(id+"F0.wireOp",EDGE,"E19.6"),sQuery(id+"F0.wireOp",EDGE,"E19.7"),sQuery(id+"F0.wireOp",EDGE,"E19.8"),sQuery(id+"F0.wireOp",EDGE,"E19.9"),sQuery(id+"F0.wireOp",EDGE,"E19.10"),sQuery(id+"F0.wireOp",EDGE,"E19.11"),sQuery(id+"F0.wireOp",EDGE,"E19.12"),sQuery(id+"F0.wireOp",EDGE,"E19.13"),sQuery(id+"F0.wireOp",EDGE,"E19.14"),sQuery(id+"F0.wireOp",EDGE,"E20.0"),sQuery(id+"F0.wireOp",EDGE,"E21.0"),sQuery(id+"F0.wireOp",EDGE,"E22.0"),sQuery(id+"F0.wireOp",EDGE,"E23.0"),sQuery(id+"F0.wireOp",EDGE,"E24.0"),sQuery(id+"F0.wireOp",EDGE,"E25.0"),sQuery(id+"F0.wireOp",EDGE,"E26.0"),sQuery(id+"F0.wireOp",EDGE,"E27.0"),sQuery(id+"F0.wireOp",EDGE,"E28.0"),sQuery(id+"F0.wireOp",EDGE,"E29.0"),sQuery(id+"F0.wireOp",EDGE,"E30.0"),sQuery(id+"F0.wireOp",EDGE,"E31.0"),sQuery(id+"F0.wireOp",EDGE,"E32.0"),sQuery(id+"F0.wireOp",EDGE,"E33.0"),sQuery(id+"F0.wireOp",EDGE,"E34.0")])],"isStart":false}),makeQuery(id+"F11.opRevolve","SWEPT_FACE",FACE,{"disambiguationData":[OSD([sQuery(id+"F10.wireOp",EDGE,"E48")])]})]});
            var Q15;
            Q15=makeQuery(id+"F21.opBoolean","INTERSECT",EDGE,{"derivedFrom":[makeQuery(id+"F2.opExtrude","CAP_FACE",FACE,{"disambiguationData":[OSD([sQuery(id+"F0.wireOp",EDGE,"E0"),sQuery(id+"F0.wireOp",EDGE,"E1"),sQuery(id+"F0.wireOp",EDGE,"E2"),sQuery(id+"F0.wireOp",EDGE,"E3"),sQuery(id+"F0.wireOp",EDGE,"E4"),sQuery(id+"F0.wireOp",EDGE,"E5"),sQuery(id+"F0.wireOp",EDGE,"E6"),sQuery(id+"F0.wireOp",EDGE,"E7"),sQuery(id+"F0.wireOp",EDGE,"E8"),sQuery(id+"F0.wireOp",EDGE,"E9"),sQuery(id+"F0.wireOp",EDGE,"E19.0"),sQuery(id+"F0.wireOp",EDGE,"E19.1"),sQuery(id+"F0.wireOp",EDGE,"E19.2"),sQuery(id+"F0.wireOp",EDGE,"E19.3"),sQuery(id+"F0.wireOp",EDGE,"E19.4"),sQuery(id+"F0.wireOp",EDGE,"E19.5"),sQuery(id+"F0.wireOp",EDGE,"E19.6"),sQuery(id+"F0.wireOp",EDGE,"E19.7"),sQuery(id+"F0.wireOp",EDGE,"E19.8"),sQuery(id+"F0.wireOp",EDGE,"E19.9"),sQuery(id+"F0.wireOp",EDGE,"E19.10"),sQuery(id+"F0.wireOp",EDGE,"E19.11"),sQuery(id+"F0.wireOp",EDGE,"E19.12"),sQuery(id+"F0.wireOp",EDGE,"E19.13"),sQuery(id+"F0.wireOp",EDGE,"E19.14"),sQuery(id+"F0.wireOp",EDGE,"E20.0"),sQuery(id+"F0.wireOp",EDGE,"E21.0"),sQuery(id+"F0.wireOp",EDGE,"E22.0"),sQuery(id+"F0.wireOp",EDGE,"E23.0"),sQuery(id+"F0.wireOp",EDGE,"E24.0"),sQuery(id+"F0.wireOp",EDGE,"E25.0"),sQuery(id+"F0.wireOp",EDGE,"E26.0"),sQuery(id+"F0.wireOp",EDGE,"E27.0"),sQuery(id+"F0.wireOp",EDGE,"E28.0"),sQuery(id+"F0.wireOp",EDGE,"E29.0"),sQuery(id+"F0.wireOp",EDGE,"E30.0"),sQuery(id+"F0.wireOp",EDGE,"E31.0"),sQuery(id+"F0.wireOp",EDGE,"E32.0"),sQuery(id+"F0.wireOp",EDGE,"E33.0"),sQuery(id+"F0.wireOp",EDGE,"E34.0")])],"isStart":false}),makeQuery(id+"F13.opRevolve","SWEPT_FACE",FACE,{"disambiguationData":[OSD([sQuery(id+"F12.wireOp",EDGE,"E51")])]})]});
            var Q16;
            Q16=makeQuery(id+"F21.opBoolean","INTERSECT",EDGE,{"derivedFrom":[makeQuery(id+"F2.opExtrude","CAP_FACE",FACE,{"disambiguationData":[OSD([sQuery(id+"F0.wireOp",EDGE,"E0"),sQuery(id+"F0.wireOp",EDGE,"E1"),sQuery(id+"F0.wireOp",EDGE,"E2"),sQuery(id+"F0.wireOp",EDGE,"E3"),sQuery(id+"F0.wireOp",EDGE,"E4"),sQuery(id+"F0.wireOp",EDGE,"E5"),sQuery(id+"F0.wireOp",EDGE,"E6"),sQuery(id+"F0.wireOp",EDGE,"E7"),sQuery(id+"F0.wireOp",EDGE,"E8"),sQuery(id+"F0.wireOp",EDGE,"E9"),sQuery(id+"F0.wireOp",EDGE,"E19.0"),sQuery(id+"F0.wireOp",EDGE,"E19.1"),sQuery(id+"F0.wireOp",EDGE,"E19.2"),sQuery(id+"F0.wireOp",EDGE,"E19.3"),sQuery(id+"F0.wireOp",EDGE,"E19.4"),sQuery(id+"F0.wireOp",EDGE,"E19.5"),sQuery(id+"F0.wireOp",EDGE,"E19.6"),sQuery(id+"F0.wireOp",EDGE,"E19.7"),sQuery(id+"F0.wireOp",EDGE,"E19.8"),sQuery(id+"F0.wireOp",EDGE,"E19.9"),sQuery(id+"F0.wireOp",EDGE,"E19.10"),sQuery(id+"F0.wireOp",EDGE,"E19.11"),sQuery(id+"F0.wireOp",EDGE,"E19.12"),sQuery(id+"F0.wireOp",EDGE,"E19.13"),sQuery(id+"F0.wireOp",EDGE,"E19.14"),sQuery(id+"F0.wireOp",EDGE,"E20.0"),sQuery(id+"F0.wireOp",EDGE,"E21.0"),sQuery(id+"F0.wireOp",EDGE,"E22.0"),sQuery(id+"F0.wireOp",EDGE,"E23.0"),sQuery(id+"F0.wireOp",EDGE,"E24.0"),sQuery(id+"F0.wireOp",EDGE,"E25.0"),sQuery(id+"F0.wireOp",EDGE,"E26.0"),sQuery(id+"F0.wireOp",EDGE,"E27.0"),sQuery(id+"F0.wireOp",EDGE,"E28.0"),sQuery(id+"F0.wireOp",EDGE,"E29.0"),sQuery(id+"F0.wireOp",EDGE,"E30.0"),sQuery(id+"F0.wireOp",EDGE,"E31.0"),sQuery(id+"F0.wireOp",EDGE,"E32.0"),sQuery(id+"F0.wireOp",EDGE,"E33.0"),sQuery(id+"F0.wireOp",EDGE,"E34.0")])],"isStart":false}),makeQuery(id+"F18.opRevolve","SWEPT_FACE",FACE,{"disambiguationData":[OSD([sQuery(id+"F16.wireOp",EDGE,"E57")])]})]});
            var Q17;
            Q17=makeQuery(id+"F21.opBoolean","INTERSECT",EDGE,{"derivedFrom":[makeQuery(id+"F2.opExtrude","CAP_FACE",FACE,{"disambiguationData":[OSD([sQuery(id+"F0.wireOp",EDGE,"E0"),sQuery(id+"F0.wireOp",EDGE,"E1"),sQuery(id+"F0.wireOp",EDGE,"E2"),sQuery(id+"F0.wireOp",EDGE,"E3"),sQuery(id+"F0.wireOp",EDGE,"E4"),sQuery(id+"F0.wireOp",EDGE,"E5"),sQuery(id+"F0.wireOp",EDGE,"E6"),sQuery(id+"F0.wireOp",EDGE,"E7"),sQuery(id+"F0.wireOp",EDGE,"E8"),sQuery(id+"F0.wireOp",EDGE,"E9"),sQuery(id+"F0.wireOp",EDGE,"E19.0"),sQuery(id+"F0.wireOp",EDGE,"E19.1"),sQuery(id+"F0.wireOp",EDGE,"E19.2"),sQuery(id+"F0.wireOp",EDGE,"E19.3"),sQuery(id+"F0.wireOp",EDGE,"E19.4"),sQuery(id+"F0.wireOp",EDGE,"E19.5"),sQuery(id+"F0.wireOp",EDGE,"E19.6"),sQuery(id+"F0.wireOp",EDGE,"E19.7"),sQuery(id+"F0.wireOp",EDGE,"E19.8"),sQuery(id+"F0.wireOp",EDGE,"E19.9"),sQuery(id+"F0.wireOp",EDGE,"E19.10"),sQuery(id+"F0.wireOp",EDGE,"E19.11"),sQuery(id+"F0.wireOp",EDGE,"E19.12"),sQuery(id+"F0.wireOp",EDGE,"E19.13"),sQuery(id+"F0.wireOp",EDGE,"E19.14"),sQuery(id+"F0.wireOp",EDGE,"E20.0"),sQuery(id+"F0.wireOp",EDGE,"E21.0"),sQuery(id+"F0.wireOp",EDGE,"E22.0"),sQuery(id+"F0.wireOp",EDGE,"E23.0"),sQuery(id+"F0.wireOp",EDGE,"E24.0"),sQuery(id+"F0.wireOp",EDGE,"E25.0"),sQuery(id+"F0.wireOp",EDGE,"E26.0"),sQuery(id+"F0.wireOp",EDGE,"E27.0"),sQuery(id+"F0.wireOp",EDGE,"E28.0"),sQuery(id+"F0.wireOp",EDGE,"E29.0"),sQuery(id+"F0.wireOp",EDGE,"E30.0"),sQuery(id+"F0.wireOp",EDGE,"E31.0"),sQuery(id+"F0.wireOp",EDGE,"E32.0"),sQuery(id+"F0.wireOp",EDGE,"E33.0"),sQuery(id+"F0.wireOp",EDGE,"E34.0")])],"isStart":false}),makeQuery(id+"F15.opRevolve","SWEPT_FACE",FACE,{"disambiguationData":[OSD([sQuery(id+"F14.wireOp",EDGE,"E54")])]})]});
            fillet(context, id + "F26", {"entities" : qUnion([Q0, Q1, Q2, Q3, Q4, Q5, Q6, Q7, Q8, Q9, Q10, Q11, Q12, Q13, Q14, Q15, Q16, Q17]), "radius" : 1.32 * mm, "tangentPropagation" : true, "allowEdgeOverflow" : false});
        }
    });
